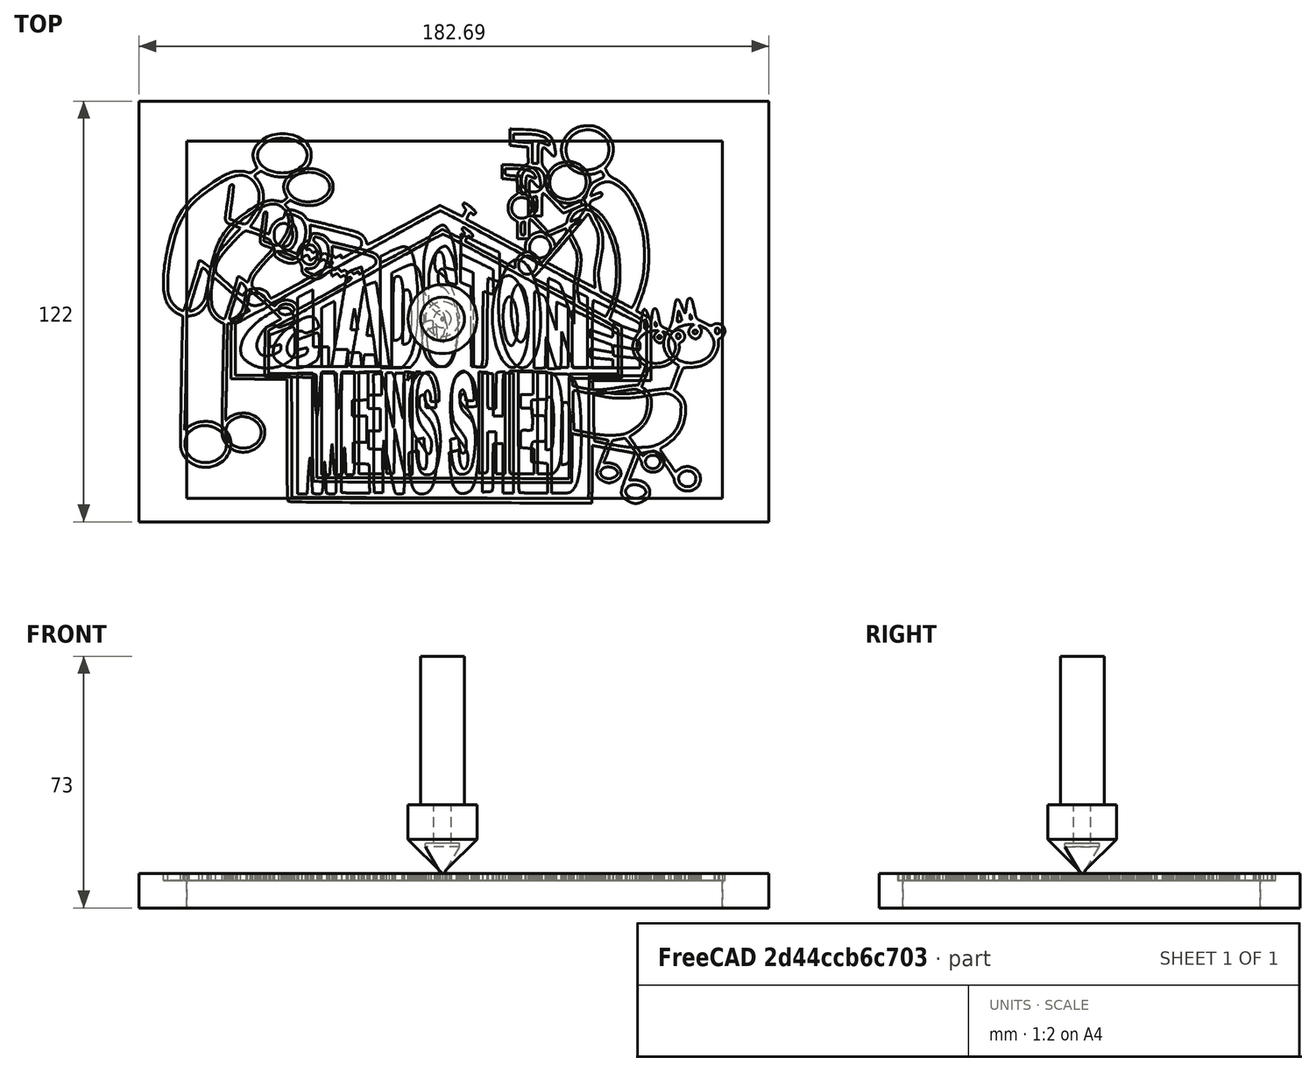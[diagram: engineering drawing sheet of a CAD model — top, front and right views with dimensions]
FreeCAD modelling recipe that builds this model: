
FCSTD DOCUMENT  (FreeCAD 0.19RUnknown)
Label: MensShedLogoVBit
License: All rights reserved
LicenseURL: http://en.wikipedia.org/wiki/All_rights_reserved
objects: Sketcher::SketchObject×20, PartDesign::Pocket×19, Path::FeaturePython×12, Part::FeaturePython×11, App::DocumentObjectGroup×6, App::FeaturePython×3, Path::FeatureCompoundPython×3, Mesh::FeaturePython×2, PartDesign::Pad×1, PartDesign::Body×1
note: 72 computed .brp shape members not serialized (recipe doc carries the construction recipe); baked Part::Feature solids carry a one-line shape summary decoded from their .brp

FEATURE [Sketcher::SketchObject] Sketch  label="M"
  FullyConstrained = false
  sketch-geometry (26):
    g0: BSplineCurve PolesCount=2 KnotsCount=2 Degree=1 IsPeriodic=0
    g1: BSplineCurve PolesCount=2 KnotsCount=2 Degree=1 IsPeriodic=0
    g2: BSplineCurve PolesCount=2 KnotsCount=2 Degree=1 IsPeriodic=0
    g3: BSplineCurve PolesCount=2 KnotsCount=2 Degree=1 IsPeriodic=0
    g4: BSplineCurve PolesCount=4 KnotsCount=2 Degree=3 IsPeriodic=0
    g5: BSplineCurve PolesCount=4 KnotsCount=2 Degree=3 IsPeriodic=0
    g6: BSplineCurve PolesCount=4 KnotsCount=2 Degree=3 IsPeriodic=0
    g7: BSplineCurve PolesCount=2 KnotsCount=2 Degree=1 IsPeriodic=0
    g8: BSplineCurve PolesCount=2 KnotsCount=2 Degree=1 IsPeriodic=0
    g9: BSplineCurve PolesCount=2 KnotsCount=2 Degree=1 IsPeriodic=0
    g10: BSplineCurve PolesCount=2 KnotsCount=2 Degree=1 IsPeriodic=0
    g11: BSplineCurve PolesCount=4 KnotsCount=2 Degree=3 IsPeriodic=0
    g12: BSplineCurve PolesCount=4 KnotsCount=2 Degree=3 IsPeriodic=0
    g13: BSplineCurve PolesCount=2 KnotsCount=2 Degree=1 IsPeriodic=0
    g14: BSplineCurve PolesCount=2 KnotsCount=2 Degree=1 IsPeriodic=0
    g15: BSplineCurve PolesCount=4 KnotsCount=2 Degree=3 IsPeriodic=0
    g16: BSplineCurve PolesCount=4 KnotsCount=2 Degree=3 IsPeriodic=0
    g17: BSplineCurve PolesCount=4 KnotsCount=2 Degree=3 IsPeriodic=0
    g18: BSplineCurve PolesCount=2 KnotsCount=2 Degree=1 IsPeriodic=0
    g19: BSplineCurve PolesCount=2 KnotsCount=2 Degree=1 IsPeriodic=0
    g20: BSplineCurve PolesCount=4 KnotsCount=2 Degree=3 IsPeriodic=0
    g21: BSplineCurve PolesCount=4 KnotsCount=2 Degree=3 IsPeriodic=0
    g22: BSplineCurve PolesCount=2 KnotsCount=2 Degree=1 IsPeriodic=0
    g23: BSplineCurve PolesCount=2 KnotsCount=2 Degree=1 IsPeriodic=0
    g24: BSplineCurve PolesCount=2 KnotsCount=2 Degree=1 IsPeriodic=0
    g25: BSplineCurve PolesCount=2 KnotsCount=2 Degree=1 IsPeriodic=0
  constraints (26):
    c: Coincident(g0,g1)
    c: Coincident(g1,g2)
    c: Coincident(g2,g3)
    c: Coincident(g3,g4)
    c: Coincident(g4,g5)
    c: Coincident(g5,g6)
    c: Coincident(g6,g7)
    c: Coincident(g7,g8)
    c: Coincident(g8,g9)
    c: Coincident(g9,g10)
    c: Coincident(g10,g11)
    c: Coincident(g11,g12)
    c: Coincident(g12,g13)
    c: Coincident(g13,g14)
    c: Coincident(g14,g15)
    c: Coincident(g15,g16)
    c: Coincident(g16,g17)
    c: Coincident(g17,g18)
    c: Coincident(g18,g19)
    c: Coincident(g19,g20)
    c: Coincident(g20,g21)
    c: Coincident(g21,g22)
    c: Coincident(g22,g23)
    c: Coincident(g23,g24)
    c: Coincident(g24,g25)
    c: Coincident(g25,g0)
FEATURE [Sketcher::SketchObject] Sketch001  label="N"
  FullyConstrained = false
  sketch-geometry (21):
    g0: BSplineCurve PolesCount=4 KnotsCount=2 Degree=3 IsPeriodic=0
    g1: BSplineCurve PolesCount=2 KnotsCount=2 Degree=1 IsPeriodic=0
    g2: BSplineCurve PolesCount=2 KnotsCount=2 Degree=1 IsPeriodic=0
    g3: BSplineCurve PolesCount=2 KnotsCount=2 Degree=1 IsPeriodic=0
    g4: BSplineCurve PolesCount=2 KnotsCount=2 Degree=1 IsPeriodic=0
    g5: BSplineCurve PolesCount=2 KnotsCount=2 Degree=1 IsPeriodic=0
    g6: BSplineCurve PolesCount=2 KnotsCount=2 Degree=1 IsPeriodic=0
    g7: BSplineCurve PolesCount=2 KnotsCount=2 Degree=1 IsPeriodic=0
    g8: BSplineCurve PolesCount=2 KnotsCount=2 Degree=1 IsPeriodic=0
    g9: BSplineCurve PolesCount=4 KnotsCount=2 Degree=3 IsPeriodic=0
    g10: BSplineCurve PolesCount=4 KnotsCount=2 Degree=3 IsPeriodic=0
    g11: BSplineCurve PolesCount=4 KnotsCount=2 Degree=3 IsPeriodic=0
    g12: BSplineCurve PolesCount=4 KnotsCount=2 Degree=3 IsPeriodic=0
    g13: BSplineCurve PolesCount=2 KnotsCount=2 Degree=1 IsPeriodic=0
    g14: BSplineCurve PolesCount=2 KnotsCount=2 Degree=1 IsPeriodic=0
    g15: BSplineCurve PolesCount=4 KnotsCount=2 Degree=3 IsPeriodic=0
    g16: BSplineCurve PolesCount=4 KnotsCount=2 Degree=3 IsPeriodic=0
    g17: BSplineCurve PolesCount=2 KnotsCount=2 Degree=1 IsPeriodic=0
    g18: BSplineCurve PolesCount=2 KnotsCount=2 Degree=1 IsPeriodic=0
    g19: BSplineCurve PolesCount=4 KnotsCount=2 Degree=3 IsPeriodic=0
    g20: BSplineCurve PolesCount=2 KnotsCount=2 Degree=1 IsPeriodic=0
  constraints (21):
    c: Coincident(g0,g1)
    c: Coincident(g1,g2)
    c: Coincident(g2,g3)
    c: Coincident(g3,g4)
    c: Coincident(g4,g5)
    c: Coincident(g5,g6)
    c: Coincident(g6,g7)
    c: Coincident(g7,g8)
    c: Coincident(g8,g9)
    c: Coincident(g9,g10)
    c: Coincident(g10,g11)
    c: Coincident(g11,g12)
    c: Coincident(g12,g13)
    c: Coincident(g13,g14)
    c: Coincident(g14,g15)
    c: Coincident(g15,g16)
    c: Coincident(g16,g17)
    c: Coincident(g17,g18)
    c: Coincident(g18,g19)
    c: Coincident(g19,g20)
    c: Coincident(g20,g0)
FEATURE [Sketcher::SketchObject] Sketch002  label="S"
  FullyConstrained = false
  sketch-geometry (25):
    g0: BSplineCurve PolesCount=4 KnotsCount=2 Degree=3 IsPeriodic=0
    g1: BSplineCurve PolesCount=4 KnotsCount=2 Degree=3 IsPeriodic=0
    g2: BSplineCurve PolesCount=4 KnotsCount=2 Degree=3 IsPeriodic=0
    g3: BSplineCurve PolesCount=2 KnotsCount=2 Degree=1 IsPeriodic=0
    g4: BSplineCurve PolesCount=2 KnotsCount=2 Degree=1 IsPeriodic=0
    g5: BSplineCurve PolesCount=4 KnotsCount=2 Degree=3 IsPeriodic=0
    g6: BSplineCurve PolesCount=4 KnotsCount=2 Degree=3 IsPeriodic=0
    g7: BSplineCurve PolesCount=4 KnotsCount=2 Degree=3 IsPeriodic=0
    g8: BSplineCurve PolesCount=4 KnotsCount=2 Degree=3 IsPeriodic=0
    g9: BSplineCurve PolesCount=4 KnotsCount=2 Degree=3 IsPeriodic=0
    g10: BSplineCurve PolesCount=4 KnotsCount=2 Degree=3 IsPeriodic=0
    g11: BSplineCurve PolesCount=4 KnotsCount=2 Degree=3 IsPeriodic=0
    g12: BSplineCurve PolesCount=4 KnotsCount=2 Degree=3 IsPeriodic=0
    g13: BSplineCurve PolesCount=2 KnotsCount=2 Degree=1 IsPeriodic=0
    g14: BSplineCurve PolesCount=2 KnotsCount=2 Degree=1 IsPeriodic=0
    g15: BSplineCurve PolesCount=2 KnotsCount=2 Degree=1 IsPeriodic=0
    g16: BSplineCurve PolesCount=2 KnotsCount=2 Degree=1 IsPeriodic=0
    g17: BSplineCurve PolesCount=4 KnotsCount=2 Degree=3 IsPeriodic=0
    g18: BSplineCurve PolesCount=4 KnotsCount=2 Degree=3 IsPeriodic=0
    g19: BSplineCurve PolesCount=4 KnotsCount=2 Degree=3 IsPeriodic=0
    g20: BSplineCurve PolesCount=4 KnotsCount=2 Degree=3 IsPeriodic=0
    g21: BSplineCurve PolesCount=4 KnotsCount=2 Degree=3 IsPeriodic=0
    g22: BSplineCurve PolesCount=4 KnotsCount=2 Degree=3 IsPeriodic=0
    g23: BSplineCurve PolesCount=4 KnotsCount=2 Degree=3 IsPeriodic=0
    g24: BSplineCurve PolesCount=2 KnotsCount=2 Degree=1 IsPeriodic=0
  constraints (25):
    c: Coincident(g0,g1)
    c: Coincident(g1,g2)
    c: Coincident(g2,g3)
    c: Coincident(g3,g4)
    c: Coincident(g4,g5)
    c: Coincident(g5,g6)
    c: Coincident(g6,g7)
    c: Coincident(g7,g8)
    c: Coincident(g8,g9)
    c: Coincident(g9,g10)
    c: Coincident(g10,g11)
    c: Coincident(g11,g12)
    c: Coincident(g12,g13)
    c: Coincident(g13,g14)
    c: Coincident(g14,g15)
    c: Coincident(g15,g16)
    c: Coincident(g16,g17)
    c: Coincident(g17,g18)
    c: Coincident(g18,g19)
    c: Coincident(g19,g20)
    c: Coincident(g20,g21)
    c: Coincident(g21,g22)
    c: Coincident(g22,g23)
    c: Coincident(g23,g24)
    c: Coincident(g24,g0)
FEATURE [Sketcher::SketchObject] Sketch003  label="S001"
  FullyConstrained = false
  sketch-geometry (24):
    g0: BSplineCurve PolesCount=4 KnotsCount=2 Degree=3 IsPeriodic=0
    g1: BSplineCurve PolesCount=2 KnotsCount=2 Degree=1 IsPeriodic=0
    g2: BSplineCurve PolesCount=2 KnotsCount=2 Degree=1 IsPeriodic=0
    g3: BSplineCurve PolesCount=4 KnotsCount=2 Degree=3 IsPeriodic=0
    g4: BSplineCurve PolesCount=4 KnotsCount=2 Degree=3 IsPeriodic=0
    g5: BSplineCurve PolesCount=4 KnotsCount=2 Degree=3 IsPeriodic=0
    g6: BSplineCurve PolesCount=4 KnotsCount=2 Degree=3 IsPeriodic=0
    g7: BSplineCurve PolesCount=4 KnotsCount=2 Degree=3 IsPeriodic=0
    g8: BSplineCurve PolesCount=4 KnotsCount=2 Degree=3 IsPeriodic=0
    g9: BSplineCurve PolesCount=4 KnotsCount=2 Degree=3 IsPeriodic=0
    g10: BSplineCurve PolesCount=4 KnotsCount=2 Degree=3 IsPeriodic=0
    g11: BSplineCurve PolesCount=4 KnotsCount=2 Degree=3 IsPeriodic=0
    g12: BSplineCurve PolesCount=4 KnotsCount=2 Degree=3 IsPeriodic=0
    g13: BSplineCurve PolesCount=4 KnotsCount=2 Degree=3 IsPeriodic=0
    g14: BSplineCurve PolesCount=2 KnotsCount=2 Degree=1 IsPeriodic=0
    g15: BSplineCurve PolesCount=2 KnotsCount=2 Degree=1 IsPeriodic=0
    g16: BSplineCurve PolesCount=4 KnotsCount=2 Degree=3 IsPeriodic=0
    g17: BSplineCurve PolesCount=4 KnotsCount=2 Degree=3 IsPeriodic=0
    g18: BSplineCurve PolesCount=4 KnotsCount=2 Degree=3 IsPeriodic=0
    g19: BSplineCurve PolesCount=4 KnotsCount=2 Degree=3 IsPeriodic=0
    g20: BSplineCurve PolesCount=4 KnotsCount=2 Degree=3 IsPeriodic=0
    g21: BSplineCurve PolesCount=4 KnotsCount=2 Degree=3 IsPeriodic=0
    g22: BSplineCurve PolesCount=4 KnotsCount=2 Degree=3 IsPeriodic=0
    g23: BSplineCurve PolesCount=2 KnotsCount=2 Degree=1 IsPeriodic=0
  constraints (24):
    c: Coincident(g0,g1)
    c: Coincident(g1,g2)
    c: Coincident(g2,g3)
    c: Coincident(g3,g4)
    c: Coincident(g4,g5)
    c: Coincident(g5,g6)
    c: Coincident(g6,g7)
    c: Coincident(g7,g8)
    c: Coincident(g8,g9)
    c: Coincident(g9,g10)
    c: Coincident(g10,g11)
    c: Coincident(g11,g12)
    c: Coincident(g12,g13)
    c: Coincident(g13,g14)
    c: Coincident(g14,g15)
    c: Coincident(g15,g16)
    c: Coincident(g16,g17)
    c: Coincident(g17,g18)
    c: Coincident(g18,g19)
    c: Coincident(g19,g20)
    c: Coincident(g20,g21)
    c: Coincident(g21,g22)
    c: Coincident(g22,g23)
    c: Coincident(g23,g0)
FEATURE [Sketcher::SketchObject] Sketch004  label="E"
  FullyConstrained = false
  sketch-geometry (24):
    g0: BSplineCurve PolesCount=4 KnotsCount=2 Degree=3 IsPeriodic=0
    g1: BSplineCurve PolesCount=4 KnotsCount=2 Degree=3 IsPeriodic=0
    g2: BSplineCurve PolesCount=2 KnotsCount=2 Degree=1 IsPeriodic=0
    g3: BSplineCurve PolesCount=2 KnotsCount=2 Degree=1 IsPeriodic=0
    g4: BSplineCurve PolesCount=2 KnotsCount=2 Degree=1 IsPeriodic=0
    g5: BSplineCurve PolesCount=2 KnotsCount=2 Degree=1 IsPeriodic=0
    g6: BSplineCurve PolesCount=2 KnotsCount=2 Degree=1 IsPeriodic=0
    g7: BSplineCurve PolesCount=2 KnotsCount=2 Degree=1 IsPeriodic=0
    g8: BSplineCurve PolesCount=2 KnotsCount=2 Degree=1 IsPeriodic=0
    g9: BSplineCurve PolesCount=2 KnotsCount=2 Degree=1 IsPeriodic=0
    g10: BSplineCurve PolesCount=2 KnotsCount=2 Degree=1 IsPeriodic=0
    g11: BSplineCurve PolesCount=2 KnotsCount=2 Degree=1 IsPeriodic=0
    g12: BSplineCurve PolesCount=2 KnotsCount=2 Degree=1 IsPeriodic=0
    g13: BSplineCurve PolesCount=2 KnotsCount=2 Degree=1 IsPeriodic=0
    g14: BSplineCurve PolesCount=2 KnotsCount=2 Degree=1 IsPeriodic=0
    g15: BSplineCurve PolesCount=2 KnotsCount=2 Degree=1 IsPeriodic=0
    g16: BSplineCurve PolesCount=2 KnotsCount=2 Degree=1 IsPeriodic=0
    g17: BSplineCurve PolesCount=2 KnotsCount=2 Degree=1 IsPeriodic=0
    g18: BSplineCurve PolesCount=2 KnotsCount=2 Degree=1 IsPeriodic=0
    g19: BSplineCurve PolesCount=2 KnotsCount=2 Degree=1 IsPeriodic=0
    g20: BSplineCurve PolesCount=2 KnotsCount=2 Degree=1 IsPeriodic=0
    g21: BSplineCurve PolesCount=2 KnotsCount=2 Degree=1 IsPeriodic=0
    g22: BSplineCurve PolesCount=4 KnotsCount=2 Degree=3 IsPeriodic=0
    g23: BSplineCurve PolesCount=2 KnotsCount=2 Degree=1 IsPeriodic=0
  constraints (24):
    c: Coincident(g0,g1)
    c: Coincident(g1,g2)
    c: Coincident(g2,g3)
    c: Coincident(g3,g4)
    c: Coincident(g4,g5)
    c: Coincident(g5,g6)
    c: Coincident(g6,g7)
    c: Coincident(g7,g8)
    c: Coincident(g8,g9)
    c: Coincident(g9,g10)
    c: Coincident(g10,g11)
    c: Coincident(g11,g12)
    c: Coincident(g12,g13)
    c: Coincident(g13,g14)
    c: Coincident(g14,g15)
    c: Coincident(g15,g16)
    c: Coincident(g16,g17)
    c: Coincident(g17,g18)
    c: Coincident(g18,g19)
    c: Coincident(g19,g20)
    c: Coincident(g20,g21)
    c: Coincident(g21,g22)
    c: Coincident(g22,g23)
    c: Coincident(g23,g0)
FEATURE [Sketcher::SketchObject] Sketch005  label="H"
  FullyConstrained = false
  sketch-geometry (24):
    g0: BSplineCurve PolesCount=2 KnotsCount=2 Degree=1 IsPeriodic=0
    g1: BSplineCurve PolesCount=2 KnotsCount=2 Degree=1 IsPeriodic=0
    g2: BSplineCurve PolesCount=2 KnotsCount=2 Degree=1 IsPeriodic=0
    g3: BSplineCurve PolesCount=2 KnotsCount=2 Degree=1 IsPeriodic=0
    g4: BSplineCurve PolesCount=4 KnotsCount=2 Degree=3 IsPeriodic=0
    g5: BSplineCurve PolesCount=4 KnotsCount=2 Degree=3 IsPeriodic=0
    g6: BSplineCurve PolesCount=2 KnotsCount=2 Degree=1 IsPeriodic=0
    g7: BSplineCurve PolesCount=2 KnotsCount=2 Degree=1 IsPeriodic=0
    g8: BSplineCurve PolesCount=2 KnotsCount=2 Degree=1 IsPeriodic=0
    g9: BSplineCurve PolesCount=2 KnotsCount=2 Degree=1 IsPeriodic=0
    g10: BSplineCurve PolesCount=2 KnotsCount=2 Degree=1 IsPeriodic=0
    g11: BSplineCurve PolesCount=2 KnotsCount=2 Degree=1 IsPeriodic=0
    g12: BSplineCurve PolesCount=2 KnotsCount=2 Degree=1 IsPeriodic=0
    g13: BSplineCurve PolesCount=2 KnotsCount=2 Degree=1 IsPeriodic=0
    g14: BSplineCurve PolesCount=2 KnotsCount=2 Degree=1 IsPeriodic=0
    g15: BSplineCurve PolesCount=2 KnotsCount=2 Degree=1 IsPeriodic=0
    g16: BSplineCurve PolesCount=4 KnotsCount=2 Degree=3 IsPeriodic=0
    g17: BSplineCurve PolesCount=4 KnotsCount=2 Degree=3 IsPeriodic=0
    g18: BSplineCurve PolesCount=2 KnotsCount=2 Degree=1 IsPeriodic=0
    g19: BSplineCurve PolesCount=2 KnotsCount=2 Degree=1 IsPeriodic=0
    g20: BSplineCurve PolesCount=2 KnotsCount=2 Degree=1 IsPeriodic=0
    g21: BSplineCurve PolesCount=2 KnotsCount=2 Degree=1 IsPeriodic=0
    g22: BSplineCurve PolesCount=2 KnotsCount=2 Degree=1 IsPeriodic=0
    g23: BSplineCurve PolesCount=2 KnotsCount=2 Degree=1 IsPeriodic=0
  constraints (24):
    c: Coincident(g0,g1)
    c: Coincident(g1,g2)
    c: Coincident(g2,g3)
    c: Coincident(g3,g4)
    c: Coincident(g4,g5)
    c: Coincident(g5,g6)
    c: Coincident(g6,g7)
    c: Coincident(g7,g8)
    c: Coincident(g8,g9)
    c: Coincident(g9,g10)
    c: Coincident(g10,g11)
    c: Coincident(g11,g12)
    c: Coincident(g12,g13)
    c: Coincident(g13,g14)
    c: Coincident(g14,g15)
    c: Coincident(g15,g16)
    c: Coincident(g16,g17)
    c: Coincident(g17,g18)
    c: Coincident(g18,g19)
    c: Coincident(g19,g20)
    c: Coincident(g20,g21)
    c: Coincident(g21,g22)
    c: Coincident(g22,g23)
    c: Coincident(g23,g0)
FEATURE [Sketcher::SketchObject] Sketch006  label="E001"
  FullyConstrained = false
  sketch-geometry (24):
    g0: BSplineCurve PolesCount=4 KnotsCount=2 Degree=3 IsPeriodic=0
    g1: BSplineCurve PolesCount=2 KnotsCount=2 Degree=1 IsPeriodic=0
    g2: BSplineCurve PolesCount=2 KnotsCount=2 Degree=1 IsPeriodic=0
    g3: BSplineCurve PolesCount=2 KnotsCount=2 Degree=1 IsPeriodic=0
    g4: BSplineCurve PolesCount=2 KnotsCount=2 Degree=1 IsPeriodic=0
    g5: BSplineCurve PolesCount=2 KnotsCount=2 Degree=1 IsPeriodic=0
    g6: BSplineCurve PolesCount=2 KnotsCount=2 Degree=1 IsPeriodic=0
    g7: BSplineCurve PolesCount=2 KnotsCount=2 Degree=1 IsPeriodic=0
    g8: BSplineCurve PolesCount=2 KnotsCount=2 Degree=1 IsPeriodic=0
    g9: BSplineCurve PolesCount=4 KnotsCount=2 Degree=3 IsPeriodic=0
    g10: BSplineCurve PolesCount=4 KnotsCount=2 Degree=3 IsPeriodic=0
    g11: BSplineCurve PolesCount=4 KnotsCount=2 Degree=3 IsPeriodic=0
    g12: BSplineCurve PolesCount=4 KnotsCount=2 Degree=3 IsPeriodic=0
    g13: BSplineCurve PolesCount=4 KnotsCount=2 Degree=3 IsPeriodic=0
    g14: BSplineCurve PolesCount=4 KnotsCount=2 Degree=3 IsPeriodic=0
    g15: BSplineCurve PolesCount=2 KnotsCount=2 Degree=1 IsPeriodic=0
    g16: BSplineCurve PolesCount=2 KnotsCount=2 Degree=1 IsPeriodic=0
    g17: BSplineCurve PolesCount=4 KnotsCount=2 Degree=3 IsPeriodic=0
    g18: BSplineCurve PolesCount=2 KnotsCount=2 Degree=1 IsPeriodic=0
    g19: BSplineCurve PolesCount=2 KnotsCount=2 Degree=1 IsPeriodic=0
    g20: BSplineCurve PolesCount=2 KnotsCount=2 Degree=1 IsPeriodic=0
    g21: BSplineCurve PolesCount=2 KnotsCount=2 Degree=1 IsPeriodic=0
    g22: BSplineCurve PolesCount=4 KnotsCount=2 Degree=3 IsPeriodic=0
    g23: BSplineCurve PolesCount=2 KnotsCount=2 Degree=1 IsPeriodic=0
  constraints (24):
    c: Coincident(g0,g1)
    c: Coincident(g1,g2)
    c: Coincident(g2,g3)
    c: Coincident(g3,g4)
    c: Coincident(g4,g5)
    c: Coincident(g5,g6)
    c: Coincident(g6,g7)
    c: Coincident(g7,g8)
    c: Coincident(g8,g9)
    c: Coincident(g9,g10)
    c: Coincident(g10,g11)
    c: Coincident(g11,g12)
    c: Coincident(g12,g13)
    c: Coincident(g13,g14)
    c: Coincident(g14,g15)
    c: Coincident(g15,g16)
    c: Coincident(g16,g17)
    c: Coincident(g17,g18)
    c: Coincident(g18,g19)
    c: Coincident(g19,g20)
    c: Coincident(g20,g21)
    c: Coincident(g21,g22)
    c: Coincident(g22,g23)
    c: Coincident(g23,g0)
FEATURE [Sketcher::SketchObject] Sketch007  label="D"
  FullyConstrained = false
  sketch-geometry (17):
    g0: BSplineCurve PolesCount=2 KnotsCount=2 Degree=1 IsPeriodic=0
    g1: BSplineCurve PolesCount=2 KnotsCount=2 Degree=1 IsPeriodic=0
    g2: BSplineCurve PolesCount=4 KnotsCount=2 Degree=3 IsPeriodic=0
    g3: BSplineCurve PolesCount=4 KnotsCount=2 Degree=3 IsPeriodic=0
    g4: BSplineCurve PolesCount=4 KnotsCount=2 Degree=3 IsPeriodic=0
    g5: BSplineCurve PolesCount=4 KnotsCount=2 Degree=3 IsPeriodic=0
    g6: BSplineCurve PolesCount=2 KnotsCount=2 Degree=1 IsPeriodic=0
    g7: BSplineCurve PolesCount=2 KnotsCount=2 Degree=1 IsPeriodic=0
    g8: BSplineCurve PolesCount=4 KnotsCount=2 Degree=3 IsPeriodic=0
    g9: BSplineCurve PolesCount=4 KnotsCount=2 Degree=3 IsPeriodic=0
    g10: BSplineCurve PolesCount=2 KnotsCount=2 Degree=1 IsPeriodic=0
    g11: BSplineCurve PolesCount=2 KnotsCount=2 Degree=1 IsPeriodic=0
    g12: BSplineCurve PolesCount=4 KnotsCount=2 Degree=3 IsPeriodic=0
    g13: BSplineCurve PolesCount=2 KnotsCount=2 Degree=1 IsPeriodic=0
    g14: BSplineCurve PolesCount=2 KnotsCount=2 Degree=1 IsPeriodic=0
    g15: BSplineCurve PolesCount=4 KnotsCount=2 Degree=3 IsPeriodic=0
    g16: BSplineCurve PolesCount=2 KnotsCount=2 Degree=1 IsPeriodic=0
  constraints (17):
    c: Coincident(g0,g1)
    c: Coincident(g1,g2)
    c: Coincident(g2,g3)
    c: Coincident(g3,g4)
    c: Coincident(g4,g5)
    c: Coincident(g5,g6)
    c: Coincident(g6,g7)
    c: Coincident(g7,g0)
    c: Coincident(g8,g9)
    c: Coincident(g9,g10)
    c: Coincident(g10,g11)
    c: Coincident(g11,g12)
    c: Coincident(g12,g13)
    c: Coincident(g13,g14)
    c: Coincident(g14,g15)
    c: Coincident(g15,g16)
    c: Coincident(g16,g8)
FEATURE [Sketcher::SketchObject] Sketch008  label="G"
  FullyConstrained = false
  sketch-geometry (24):
    g0: BSplineCurve PolesCount=4 KnotsCount=2 Degree=3 IsPeriodic=0
    g1: BSplineCurve PolesCount=4 KnotsCount=2 Degree=3 IsPeriodic=0
    g2: BSplineCurve PolesCount=4 KnotsCount=2 Degree=3 IsPeriodic=0
    g3: BSplineCurve PolesCount=4 KnotsCount=2 Degree=3 IsPeriodic=0
    g4: BSplineCurve PolesCount=4 KnotsCount=2 Degree=3 IsPeriodic=0
    g5: BSplineCurve PolesCount=4 KnotsCount=2 Degree=3 IsPeriodic=0
    g6: BSplineCurve PolesCount=4 KnotsCount=2 Degree=3 IsPeriodic=0
    g7: BSplineCurve PolesCount=4 KnotsCount=2 Degree=3 IsPeriodic=0
    g8: BSplineCurve PolesCount=4 KnotsCount=2 Degree=3 IsPeriodic=0
    g9: BSplineCurve PolesCount=4 KnotsCount=2 Degree=3 IsPeriodic=0
    g10: BSplineCurve PolesCount=4 KnotsCount=2 Degree=3 IsPeriodic=0
    g11: BSplineCurve PolesCount=4 KnotsCount=2 Degree=3 IsPeriodic=0
    g12: BSplineCurve PolesCount=4 KnotsCount=2 Degree=3 IsPeriodic=0
    g13: BSplineCurve PolesCount=4 KnotsCount=2 Degree=3 IsPeriodic=0
    g14: BSplineCurve PolesCount=2 KnotsCount=2 Degree=1 IsPeriodic=0
    g15: BSplineCurve PolesCount=2 KnotsCount=2 Degree=1 IsPeriodic=0
    g16: BSplineCurve PolesCount=2 KnotsCount=2 Degree=1 IsPeriodic=0
    g17: BSplineCurve PolesCount=2 KnotsCount=2 Degree=1 IsPeriodic=0
    g18: BSplineCurve PolesCount=4 KnotsCount=2 Degree=3 IsPeriodic=0
    g19: BSplineCurve PolesCount=4 KnotsCount=2 Degree=3 IsPeriodic=0
    g20: BSplineCurve PolesCount=2 KnotsCount=2 Degree=1 IsPeriodic=0
    g21: BSplineCurve PolesCount=2 KnotsCount=2 Degree=1 IsPeriodic=0
    g22: BSplineCurve PolesCount=4 KnotsCount=2 Degree=3 IsPeriodic=0
    g23: BSplineCurve PolesCount=2 KnotsCount=2 Degree=1 IsPeriodic=0
  constraints (24):
    c: Coincident(g0,g1)
    c: Coincident(g1,g2)
    c: Coincident(g2,g3)
    c: Coincident(g3,g4)
    c: Coincident(g4,g5)
    c: Coincident(g5,g6)
    c: Coincident(g6,g7)
    c: Coincident(g7,g8)
    c: Coincident(g8,g9)
    c: Coincident(g9,g10)
    c: Coincident(g10,g11)
    c: Coincident(g11,g12)
    c: Coincident(g12,g13)
    c: Coincident(g13,g14)
    c: Coincident(g14,g15)
    c: Coincident(g15,g16)
    c: Coincident(g16,g17)
    c: Coincident(g17,g18)
    c: Coincident(g18,g19)
    c: Coincident(g19,g20)
    c: Coincident(g20,g21)
    c: Coincident(g21,g22)
    c: Coincident(g22,g23)
    c: Coincident(g23,g0)
FEATURE [Sketcher::SketchObject] Sketch009  label="N001"
  FullyConstrained = false
  sketch-geometry (21):
    g0: BSplineCurve PolesCount=4 KnotsCount=2 Degree=3 IsPeriodic=0
    g1: BSplineCurve PolesCount=4 KnotsCount=2 Degree=3 IsPeriodic=0
    g2: BSplineCurve PolesCount=4 KnotsCount=2 Degree=3 IsPeriodic=0
    g3: BSplineCurve PolesCount=4 KnotsCount=2 Degree=3 IsPeriodic=0
    g4: BSplineCurve PolesCount=2 KnotsCount=2 Degree=1 IsPeriodic=0
    g5: BSplineCurve PolesCount=2 KnotsCount=2 Degree=1 IsPeriodic=0
    g6: BSplineCurve PolesCount=4 KnotsCount=2 Degree=3 IsPeriodic=0
    g7: BSplineCurve PolesCount=4 KnotsCount=2 Degree=3 IsPeriodic=0
    g8: BSplineCurve PolesCount=2 KnotsCount=2 Degree=1 IsPeriodic=0
    g9: BSplineCurve PolesCount=2 KnotsCount=2 Degree=1 IsPeriodic=0
    g10: BSplineCurve PolesCount=2 KnotsCount=2 Degree=1 IsPeriodic=0
    g11: BSplineCurve PolesCount=2 KnotsCount=2 Degree=1 IsPeriodic=0
    g12: BSplineCurve PolesCount=2 KnotsCount=2 Degree=1 IsPeriodic=0
    g13: BSplineCurve PolesCount=2 KnotsCount=2 Degree=1 IsPeriodic=0
    g14: BSplineCurve PolesCount=2 KnotsCount=2 Degree=1 IsPeriodic=0
    g15: BSplineCurve PolesCount=2 KnotsCount=2 Degree=1 IsPeriodic=0
    g16: BSplineCurve PolesCount=2 KnotsCount=2 Degree=1 IsPeriodic=0
    g17: BSplineCurve PolesCount=2 KnotsCount=2 Degree=1 IsPeriodic=0
    g18: BSplineCurve PolesCount=2 KnotsCount=2 Degree=1 IsPeriodic=0
    g19: BSplineCurve PolesCount=2 KnotsCount=2 Degree=1 IsPeriodic=0
    g20: BSplineCurve PolesCount=2 KnotsCount=2 Degree=1 IsPeriodic=0
  constraints (21):
    c: Coincident(g0,g1)
    c: Coincident(g1,g2)
    c: Coincident(g2,g3)
    c: Coincident(g3,g4)
    c: Coincident(g4,g5)
    c: Coincident(g5,g6)
    c: Coincident(g6,g7)
    c: Coincident(g7,g8)
    c: Coincident(g8,g9)
    c: Coincident(g9,g10)
    c: Coincident(g10,g11)
    c: Coincident(g11,g12)
    c: Coincident(g12,g13)
    c: Coincident(g13,g14)
    c: Coincident(g14,g15)
    c: Coincident(g15,g16)
    c: Coincident(g16,g17)
    c: Coincident(g17,g18)
    c: Coincident(g18,g19)
    c: Coincident(g19,g20)
    c: Coincident(g20,g0)
FEATURE [Sketcher::SketchObject] Sketch010  label="D001"
  FullyConstrained = false
  sketch-geometry (18):
    g0: BSplineCurve PolesCount=2 KnotsCount=2 Degree=1 IsPeriodic=0
    g1: BSplineCurve PolesCount=2 KnotsCount=2 Degree=1 IsPeriodic=0
    g2: BSplineCurve PolesCount=4 KnotsCount=2 Degree=3 IsPeriodic=0
    g3: BSplineCurve PolesCount=4 KnotsCount=2 Degree=3 IsPeriodic=0
    g4: BSplineCurve PolesCount=4 KnotsCount=2 Degree=3 IsPeriodic=0
    g5: BSplineCurve PolesCount=4 KnotsCount=2 Degree=3 IsPeriodic=0
    g6: BSplineCurve PolesCount=2 KnotsCount=2 Degree=1 IsPeriodic=0
    g7: BSplineCurve PolesCount=2 KnotsCount=2 Degree=1 IsPeriodic=0
    g8: BSplineCurve PolesCount=2 KnotsCount=2 Degree=1 IsPeriodic=0
    g9: BSplineCurve PolesCount=2 KnotsCount=2 Degree=1 IsPeriodic=0
    g10: BSplineCurve PolesCount=4 KnotsCount=2 Degree=3 IsPeriodic=0
    g11: BSplineCurve PolesCount=4 KnotsCount=2 Degree=3 IsPeriodic=0
    g12: BSplineCurve PolesCount=4 KnotsCount=2 Degree=3 IsPeriodic=0
    g13: BSplineCurve PolesCount=4 KnotsCount=2 Degree=3 IsPeriodic=0
    g14: BSplineCurve PolesCount=4 KnotsCount=2 Degree=3 IsPeriodic=0
    g15: BSplineCurve PolesCount=2 KnotsCount=2 Degree=1 IsPeriodic=0
    g16: BSplineCurve PolesCount=2 KnotsCount=2 Degree=1 IsPeriodic=0
    g17: BSplineCurve PolesCount=4 KnotsCount=2 Degree=3 IsPeriodic=0
  constraints (18):
    c: Coincident(g0,g1)
    c: Coincident(g1,g2)
    c: Coincident(g2,g3)
    c: Coincident(g3,g4)
    c: Coincident(g4,g5)
    c: Coincident(g5,g6)
    c: Coincident(g6,g7)
    c: Coincident(g7,g8)
    c: Coincident(g8,g9)
    c: Coincident(g9,g0)
    c: Coincident(g10,g11)
    c: Coincident(g11,g12)
    c: Coincident(g12,g13)
    c: Coincident(g13,g14)
    c: Coincident(g14,g15)
    c: Coincident(g15,g16)
    c: Coincident(g16,g17)
    c: Coincident(g17,g10)
FEATURE [Sketcher::SketchObject] Sketch011  label="T"
  FullyConstrained = false
  sketch-geometry (16):
    g0: BSplineCurve PolesCount=2 KnotsCount=2 Degree=1 IsPeriodic=0
    g1: BSplineCurve PolesCount=2 KnotsCount=2 Degree=1 IsPeriodic=0
    g2: BSplineCurve PolesCount=2 KnotsCount=2 Degree=1 IsPeriodic=0
    g3: BSplineCurve PolesCount=2 KnotsCount=2 Degree=1 IsPeriodic=0
    g4: BSplineCurve PolesCount=2 KnotsCount=2 Degree=1 IsPeriodic=0
    g5: BSplineCurve PolesCount=2 KnotsCount=2 Degree=1 IsPeriodic=0
    g6: BSplineCurve PolesCount=2 KnotsCount=2 Degree=1 IsPeriodic=0
    g7: BSplineCurve PolesCount=2 KnotsCount=2 Degree=1 IsPeriodic=0
    g8: BSplineCurve PolesCount=4 KnotsCount=2 Degree=3 IsPeriodic=0
    g9: BSplineCurve PolesCount=2 KnotsCount=2 Degree=1 IsPeriodic=0
    g10: BSplineCurve PolesCount=2 KnotsCount=2 Degree=1 IsPeriodic=0
    g11: BSplineCurve PolesCount=4 KnotsCount=2 Degree=3 IsPeriodic=0
    g12: BSplineCurve PolesCount=4 KnotsCount=2 Degree=3 IsPeriodic=0
    g13: BSplineCurve PolesCount=4 KnotsCount=2 Degree=3 IsPeriodic=0
    g14: BSplineCurve PolesCount=4 KnotsCount=2 Degree=3 IsPeriodic=0
    g15: BSplineCurve PolesCount=2 KnotsCount=2 Degree=1 IsPeriodic=0
  constraints (16):
    c: Coincident(g0,g1)
    c: Coincident(g1,g2)
    c: Coincident(g2,g3)
    c: Coincident(g3,g4)
    c: Coincident(g4,g5)
    c: Coincident(g5,g6)
    c: Coincident(g6,g7)
    c: Coincident(g7,g8)
    c: Coincident(g8,g9)
    c: Coincident(g9,g10)
    c: Coincident(g10,g11)
    c: Coincident(g11,g12)
    c: Coincident(g12,g13)
    c: Coincident(g13,g14)
    c: Coincident(g14,g15)
    c: Coincident(g15,g0)
FEATURE [Sketcher::SketchObject] Sketch012  label="O"
  FullyConstrained = false
  sketch-geometry (8):
    g0: BSplineCurve PolesCount=4 KnotsCount=2 Degree=3 IsPeriodic=0
    g1: BSplineCurve PolesCount=4 KnotsCount=2 Degree=3 IsPeriodic=0
    g2: BSplineCurve PolesCount=4 KnotsCount=2 Degree=3 IsPeriodic=0
    g3: BSplineCurve PolesCount=4 KnotsCount=2 Degree=3 IsPeriodic=0
    g4: BSplineCurve PolesCount=4 KnotsCount=2 Degree=3 IsPeriodic=0
    g5: BSplineCurve PolesCount=4 KnotsCount=2 Degree=3 IsPeriodic=0
    g6: BSplineCurve PolesCount=4 KnotsCount=2 Degree=3 IsPeriodic=0
    g7: BSplineCurve PolesCount=4 KnotsCount=2 Degree=3 IsPeriodic=0
  constraints (8):
    c: Coincident(g0,g1)
    c: Coincident(g1,g2)
    c: Coincident(g2,g3)
    c: Coincident(g3,g0)
    c: Coincident(g4,g5)
    c: Coincident(g5,g6)
    c: Coincident(g6,g7)
    c: Coincident(g7,g4)
FEATURE [Sketcher::SketchObject] Sketch013  label="E002"
  FullyConstrained = false
  sketch-geometry (24):
    g0: BSplineCurve PolesCount=4 KnotsCount=2 Degree=3 IsPeriodic=0
    g1: BSplineCurve PolesCount=4 KnotsCount=2 Degree=3 IsPeriodic=0
    g2: BSplineCurve PolesCount=4 KnotsCount=2 Degree=3 IsPeriodic=0
    g3: BSplineCurve PolesCount=4 KnotsCount=2 Degree=3 IsPeriodic=0
    g4: BSplineCurve PolesCount=4 KnotsCount=2 Degree=3 IsPeriodic=0
    g5: BSplineCurve PolesCount=4 KnotsCount=2 Degree=3 IsPeriodic=0
    g6: BSplineCurve PolesCount=4 KnotsCount=2 Degree=3 IsPeriodic=0
    g7: BSplineCurve PolesCount=4 KnotsCount=2 Degree=3 IsPeriodic=0
    g8: BSplineCurve PolesCount=2 KnotsCount=2 Degree=1 IsPeriodic=0
    g9: BSplineCurve PolesCount=2 KnotsCount=2 Degree=1 IsPeriodic=0
    g10: BSplineCurve PolesCount=4 KnotsCount=2 Degree=3 IsPeriodic=0
    g11: BSplineCurve PolesCount=4 KnotsCount=2 Degree=3 IsPeriodic=0
    g12: BSplineCurve PolesCount=4 KnotsCount=2 Degree=3 IsPeriodic=0
    g13: BSplineCurve PolesCount=4 KnotsCount=2 Degree=3 IsPeriodic=0
    g14: BSplineCurve PolesCount=4 KnotsCount=2 Degree=3 IsPeriodic=0
    g15: BSplineCurve PolesCount=2 KnotsCount=2 Degree=1 IsPeriodic=0
    g16: BSplineCurve PolesCount=2 KnotsCount=2 Degree=1 IsPeriodic=0
    g17: BSplineCurve PolesCount=4 KnotsCount=2 Degree=3 IsPeriodic=0
    g18: BSplineCurve PolesCount=2 KnotsCount=2 Degree=1 IsPeriodic=0
    g19: BSplineCurve PolesCount=2 KnotsCount=2 Degree=1 IsPeriodic=0
    g20: BSplineCurve PolesCount=2 KnotsCount=2 Degree=1 IsPeriodic=0
    g21: BSplineCurve PolesCount=2 KnotsCount=2 Degree=1 IsPeriodic=0
    g22: BSplineCurve PolesCount=2 KnotsCount=2 Degree=1 IsPeriodic=0
    g23: BSplineCurve PolesCount=2 KnotsCount=2 Degree=1 IsPeriodic=0
  constraints (24):
    c: Coincident(g0,g1)
    c: Coincident(g1,g2)
    c: Coincident(g2,g3)
    c: Coincident(g3,g4)
    c: Coincident(g4,g5)
    c: Coincident(g5,g6)
    c: Coincident(g6,g7)
    c: Coincident(g7,g8)
    c: Coincident(g8,g9)
    c: Coincident(g9,g10)
    c: Coincident(g10,g11)
    c: Coincident(g11,g12)
    c: Coincident(g12,g13)
    c: Coincident(g13,g14)
    c: Coincident(g14,g15)
    c: Coincident(g15,g16)
    c: Coincident(g16,g17)
    c: Coincident(g17,g18)
    c: Coincident(g18,g19)
    c: Coincident(g19,g20)
    c: Coincident(g20,g21)
    c: Coincident(g21,g22)
    c: Coincident(g22,g23)
    c: Coincident(g23,g0)
FEATURE [Sketcher::SketchObject] Sketch014  label="L"
  FullyConstrained = false
  sketch-geometry (12):
    g0: BSplineCurve PolesCount=2 KnotsCount=2 Degree=1 IsPeriodic=0
    g1: BSplineCurve PolesCount=2 KnotsCount=2 Degree=1 IsPeriodic=0
    g2: BSplineCurve PolesCount=4 KnotsCount=2 Degree=3 IsPeriodic=0
    g3: BSplineCurve PolesCount=4 KnotsCount=2 Degree=3 IsPeriodic=0
    g4: BSplineCurve PolesCount=2 KnotsCount=2 Degree=1 IsPeriodic=0
    g5: BSplineCurve PolesCount=2 KnotsCount=2 Degree=1 IsPeriodic=0
    g6: BSplineCurve PolesCount=2 KnotsCount=2 Degree=1 IsPeriodic=0
    g7: BSplineCurve PolesCount=2 KnotsCount=2 Degree=1 IsPeriodic=0
    g8: BSplineCurve PolesCount=2 KnotsCount=2 Degree=1 IsPeriodic=0
    g9: BSplineCurve PolesCount=2 KnotsCount=2 Degree=1 IsPeriodic=0
    g10: BSplineCurve PolesCount=2 KnotsCount=2 Degree=1 IsPeriodic=0
    g11: BSplineCurve PolesCount=2 KnotsCount=2 Degree=1 IsPeriodic=0
  constraints (12):
    c: Coincident(g0,g1)
    c: Coincident(g1,g2)
    c: Coincident(g2,g3)
    c: Coincident(g3,g4)
    c: Coincident(g4,g5)
    c: Coincident(g5,g6)
    c: Coincident(g6,g7)
    c: Coincident(g7,g8)
    c: Coincident(g8,g9)
    c: Coincident(g9,g10)
    c: Coincident(g10,g11)
    c: Coincident(g11,g0)
FEATURE [Sketcher::SketchObject] Sketch015  label="A"
  FullyConstrained = false
  sketch-geometry (23):
    g0: BSplineCurve PolesCount=4 KnotsCount=2 Degree=3 IsPeriodic=0
    g1: BSplineCurve PolesCount=4 KnotsCount=2 Degree=3 IsPeriodic=0
    g2: BSplineCurve PolesCount=4 KnotsCount=2 Degree=3 IsPeriodic=0
    g3: BSplineCurve PolesCount=4 KnotsCount=2 Degree=3 IsPeriodic=0
    g4: BSplineCurve PolesCount=4 KnotsCount=2 Degree=3 IsPeriodic=0
    g5: BSplineCurve PolesCount=4 KnotsCount=2 Degree=3 IsPeriodic=0
    g6: BSplineCurve PolesCount=2 KnotsCount=2 Degree=1 IsPeriodic=0
    g7: BSplineCurve PolesCount=2 KnotsCount=2 Degree=1 IsPeriodic=0
    g8: BSplineCurve PolesCount=4 KnotsCount=2 Degree=3 IsPeriodic=0
    g9: BSplineCurve PolesCount=4 KnotsCount=2 Degree=3 IsPeriodic=0
    g10: BSplineCurve PolesCount=2 KnotsCount=2 Degree=1 IsPeriodic=0
    g11: BSplineCurve PolesCount=2 KnotsCount=2 Degree=1 IsPeriodic=0
    g12: BSplineCurve PolesCount=2 KnotsCount=2 Degree=1 IsPeriodic=0
    g13: BSplineCurve PolesCount=2 KnotsCount=2 Degree=1 IsPeriodic=0
    g14: BSplineCurve PolesCount=4 KnotsCount=2 Degree=3 IsPeriodic=0
    g15: BSplineCurve PolesCount=4 KnotsCount=2 Degree=3 IsPeriodic=0
    g16: BSplineCurve PolesCount=2 KnotsCount=2 Degree=1 IsPeriodic=0
    g17: BSplineCurve PolesCount=2 KnotsCount=2 Degree=1 IsPeriodic=0
    g18: BSplineCurve PolesCount=4 KnotsCount=2 Degree=3 IsPeriodic=0
    g19: BSplineCurve PolesCount=2 KnotsCount=2 Degree=1 IsPeriodic=0
    g20: BSplineCurve PolesCount=2 KnotsCount=2 Degree=1 IsPeriodic=0
    g21: BSplineCurve PolesCount=2 KnotsCount=2 Degree=1 IsPeriodic=0
    g22: BSplineCurve PolesCount=2 KnotsCount=2 Degree=1 IsPeriodic=0
  constraints (23):
    c: Coincident(g0,g1)
    c: Coincident(g1,g2)
    c: Coincident(g2,g3)
    c: Coincident(g3,g4)
    c: Coincident(g4,g5)
    c: Coincident(g5,g6)
    c: Coincident(g6,g7)
    c: Coincident(g7,g8)
    c: Coincident(g8,g9)
    c: Coincident(g9,g10)
    c: Coincident(g10,g11)
    c: Coincident(g11,g12)
    c: Coincident(g12,g13)
    c: Coincident(g13,g14)
    c: Coincident(g14,g0)
    c: Coincident(g15,g16)
    c: Coincident(g16,g17)
    c: Coincident(g17,g18)
    c: Coincident(g18,g19)
    c: Coincident(g19,g20)
    c: Coincident(g20,g21)
    c: Coincident(g21,g22)
    c: Coincident(g22,g15)
FEATURE [Sketcher::SketchObject] Sketch016  label="S002"
  FullyConstrained = false
  sketch-geometry (26):
    g0: BSplineCurve PolesCount=4 KnotsCount=2 Degree=3 IsPeriodic=0
    g1: BSplineCurve PolesCount=4 KnotsCount=2 Degree=3 IsPeriodic=0
    g2: BSplineCurve PolesCount=4 KnotsCount=2 Degree=3 IsPeriodic=0
    g3: BSplineCurve PolesCount=4 KnotsCount=2 Degree=3 IsPeriodic=0
    g4: BSplineCurve PolesCount=4 KnotsCount=2 Degree=3 IsPeriodic=0
    g5: BSplineCurve PolesCount=4 KnotsCount=2 Degree=3 IsPeriodic=0
    g6: BSplineCurve PolesCount=4 KnotsCount=2 Degree=3 IsPeriodic=0
    g7: BSplineCurve PolesCount=4 KnotsCount=2 Degree=3 IsPeriodic=0
    g8: BSplineCurve PolesCount=4 KnotsCount=2 Degree=3 IsPeriodic=0
    g9: BSplineCurve PolesCount=4 KnotsCount=2 Degree=3 IsPeriodic=0
    g10: BSplineCurve PolesCount=4 KnotsCount=2 Degree=3 IsPeriodic=0
    g11: BSplineCurve PolesCount=4 KnotsCount=2 Degree=3 IsPeriodic=0
    g12: BSplineCurve PolesCount=4 KnotsCount=2 Degree=3 IsPeriodic=0
    g13: BSplineCurve PolesCount=4 KnotsCount=2 Degree=3 IsPeriodic=0
    g14: BSplineCurve PolesCount=4 KnotsCount=2 Degree=3 IsPeriodic=0
    g15: BSplineCurve PolesCount=2 KnotsCount=2 Degree=1 IsPeriodic=0
    g16: BSplineCurve PolesCount=2 KnotsCount=2 Degree=1 IsPeriodic=0
    g17: BSplineCurve PolesCount=4 KnotsCount=2 Degree=3 IsPeriodic=0
    g18: BSplineCurve PolesCount=4 KnotsCount=2 Degree=3 IsPeriodic=0
    g19: BSplineCurve PolesCount=4 KnotsCount=2 Degree=3 IsPeriodic=0
    g20: BSplineCurve PolesCount=4 KnotsCount=2 Degree=3 IsPeriodic=0
    g21: BSplineCurve PolesCount=4 KnotsCount=2 Degree=3 IsPeriodic=0
    g22: BSplineCurve PolesCount=4 KnotsCount=2 Degree=3 IsPeriodic=0
    g23: BSplineCurve PolesCount=4 KnotsCount=2 Degree=3 IsPeriodic=0
    g24: BSplineCurve PolesCount=4 KnotsCount=2 Degree=3 IsPeriodic=0
    g25: BSplineCurve PolesCount=2 KnotsCount=2 Degree=1 IsPeriodic=0
  constraints (26):
    c: Coincident(g0,g1)
    c: Coincident(g1,g2)
    c: Coincident(g2,g3)
    c: Coincident(g3,g4)
    c: Coincident(g4,g5)
    c: Coincident(g5,g6)
    c: Coincident(g6,g7)
    c: Coincident(g7,g8)
    c: Coincident(g8,g9)
    c: Coincident(g9,g10)
    c: Coincident(g10,g11)
    c: Coincident(g11,g12)
    c: Coincident(g12,g13)
    c: Coincident(g13,g14)
    c: Coincident(g14,g15)
    c: Coincident(g15,g16)
    c: Coincident(g16,g17)
    c: Coincident(g17,g18)
    c: Coincident(g18,g19)
    c: Coincident(g19,g20)
    c: Coincident(g20,g21)
    c: Coincident(g21,g22)
    c: Coincident(g22,g23)
    c: Coincident(g23,g24)
    c: Coincident(g24,g25)
    c: Coincident(g25,g0)
FEATURE [Sketcher::SketchObject] Sketch017  label="House"
  FullyConstrained = false
  MapMode = 5
  Support = -> [XY_Plane]
  sketch-geometry (422):
    g0: BSplineCurve PolesCount=4 KnotsCount=2 Degree=3 IsPeriodic=0
    g1: BSplineCurve PolesCount=4 KnotsCount=2 Degree=3 IsPeriodic=0
    g2: BSplineCurve PolesCount=2 KnotsCount=2 Degree=1 IsPeriodic=0
    g3: BSplineCurve PolesCount=2 KnotsCount=2 Degree=1 IsPeriodic=0
    g4: BSplineCurve PolesCount=2 KnotsCount=2 Degree=1 IsPeriodic=0
    g5: BSplineCurve PolesCount=2 KnotsCount=2 Degree=1 IsPeriodic=0
    g6: BSplineCurve PolesCount=4 KnotsCount=2 Degree=3 IsPeriodic=0
    g7: BSplineCurve PolesCount=2 KnotsCount=2 Degree=1 IsPeriodic=0
    g8: BSplineCurve PolesCount=2 KnotsCount=2 Degree=1 IsPeriodic=0
    g9: BSplineCurve PolesCount=2 KnotsCount=2 Degree=1 IsPeriodic=0
    g10: BSplineCurve PolesCount=2 KnotsCount=2 Degree=1 IsPeriodic=0
    g11: BSplineCurve PolesCount=4 KnotsCount=2 Degree=3 IsPeriodic=0
    g12: BSplineCurve PolesCount=4 KnotsCount=2 Degree=3 IsPeriodic=0
    g13: BSplineCurve PolesCount=4 KnotsCount=2 Degree=3 IsPeriodic=0
    g14: BSplineCurve PolesCount=2 KnotsCount=2 Degree=1 IsPeriodic=0
    g15: BSplineCurve PolesCount=2 KnotsCount=2 Degree=1 IsPeriodic=0
    g16: BSplineCurve PolesCount=4 KnotsCount=2 Degree=3 IsPeriodic=0
    g17: BSplineCurve PolesCount=2 KnotsCount=2 Degree=1 IsPeriodic=0
    g18: BSplineCurve PolesCount=2 KnotsCount=2 Degree=1 IsPeriodic=0
    g19: BSplineCurve PolesCount=4 KnotsCount=2 Degree=3 IsPeriodic=0
    g20: BSplineCurve PolesCount=4 KnotsCount=2 Degree=3 IsPeriodic=0
    g21: BSplineCurve PolesCount=4 KnotsCount=2 Degree=3 IsPeriodic=0
    g22: BSplineCurve PolesCount=4 KnotsCount=2 Degree=3 IsPeriodic=0
    g23: BSplineCurve PolesCount=4 KnotsCount=2 Degree=3 IsPeriodic=0
    g24: BSplineCurve PolesCount=4 KnotsCount=2 Degree=3 IsPeriodic=0
    g25: BSplineCurve PolesCount=2 KnotsCount=2 Degree=1 IsPeriodic=0
    g26: BSplineCurve PolesCount=2 KnotsCount=2 Degree=1 IsPeriodic=0
    g27: BSplineCurve PolesCount=4 KnotsCount=2 Degree=3 IsPeriodic=0
    g28: BSplineCurve PolesCount=4 KnotsCount=2 Degree=3 IsPeriodic=0
    g29: BSplineCurve PolesCount=4 KnotsCount=2 Degree=3 IsPeriodic=0
    g30: BSplineCurve PolesCount=4 KnotsCount=2 Degree=3 IsPeriodic=0
    g31: BSplineCurve PolesCount=4 KnotsCount=2 Degree=3 IsPeriodic=0
    g32: BSplineCurve PolesCount=2 KnotsCount=2 Degree=1 IsPeriodic=0
    g33: BSplineCurve PolesCount=2 KnotsCount=2 Degree=1 IsPeriodic=0
    g34: BSplineCurve PolesCount=4 KnotsCount=2 Degree=3 IsPeriodic=0
    g35: BSplineCurve PolesCount=4 KnotsCount=2 Degree=3 IsPeriodic=0
    g36: BSplineCurve PolesCount=4 KnotsCount=2 Degree=3 IsPeriodic=0
    g37: BSplineCurve PolesCount=4 KnotsCount=2 Degree=3 IsPeriodic=0
    g38: BSplineCurve PolesCount=4 KnotsCount=2 Degree=3 IsPeriodic=0
    g39: BSplineCurve PolesCount=2 KnotsCount=2 Degree=1 IsPeriodic=0
    g40: BSplineCurve PolesCount=2 KnotsCount=2 Degree=1 IsPeriodic=0
    g41: BSplineCurve PolesCount=4 KnotsCount=2 Degree=3 IsPeriodic=0
    g42: BSplineCurve PolesCount=4 KnotsCount=2 Degree=3 IsPeriodic=0
    g43: BSplineCurve PolesCount=4 KnotsCount=2 Degree=3 IsPeriodic=0
    g44: BSplineCurve PolesCount=4 KnotsCount=2 Degree=3 IsPeriodic=0
    g45: BSplineCurve PolesCount=4 KnotsCount=2 Degree=3 IsPeriodic=0
    g46: BSplineCurve PolesCount=4 KnotsCount=2 Degree=3 IsPeriodic=0
    g47: BSplineCurve PolesCount=4 KnotsCount=2 Degree=3 IsPeriodic=0
    g48: BSplineCurve PolesCount=4 KnotsCount=2 Degree=3 IsPeriodic=0
    g49: BSplineCurve PolesCount=4 KnotsCount=2 Degree=3 IsPeriodic=0
    g50: BSplineCurve PolesCount=4 KnotsCount=2 Degree=3 IsPeriodic=0
    g51: BSplineCurve PolesCount=4 KnotsCount=2 Degree=3 IsPeriodic=0
    g52: BSplineCurve PolesCount=4 KnotsCount=2 Degree=3 IsPeriodic=0
    g53: BSplineCurve PolesCount=4 KnotsCount=2 Degree=3 IsPeriodic=0
    g54: BSplineCurve PolesCount=4 KnotsCount=2 Degree=3 IsPeriodic=0
    g55: BSplineCurve PolesCount=4 KnotsCount=2 Degree=3 IsPeriodic=0
    g56: BSplineCurve PolesCount=4 KnotsCount=2 Degree=3 IsPeriodic=0
    g57: BSplineCurve PolesCount=2 KnotsCount=2 Degree=1 IsPeriodic=0
    g58: BSplineCurve PolesCount=2 KnotsCount=2 Degree=1 IsPeriodic=0
    g59: BSplineCurve PolesCount=4 KnotsCount=2 Degree=3 IsPeriodic=0
    g60: BSplineCurve PolesCount=4 KnotsCount=2 Degree=3 IsPeriodic=0
    g61: BSplineCurve PolesCount=4 KnotsCount=2 Degree=3 IsPeriodic=0
    g62: BSplineCurve PolesCount=4 KnotsCount=2 Degree=3 IsPeriodic=0
    g63: BSplineCurve PolesCount=4 KnotsCount=2 Degree=3 IsPeriodic=0
    g64: BSplineCurve PolesCount=4 KnotsCount=2 Degree=3 IsPeriodic=0
    g65: BSplineCurve PolesCount=4 KnotsCount=2 Degree=3 IsPeriodic=0
    g66: BSplineCurve PolesCount=4 KnotsCount=2 Degree=3 IsPeriodic=0
    g67: BSplineCurve PolesCount=4 KnotsCount=2 Degree=3 IsPeriodic=0
    g68: BSplineCurve PolesCount=2 KnotsCount=2 Degree=1 IsPeriodic=0
    g69: BSplineCurve PolesCount=2 KnotsCount=2 Degree=1 IsPeriodic=0
    g70: BSplineCurve PolesCount=4 KnotsCount=2 Degree=3 IsPeriodic=0
    g71: BSplineCurve PolesCount=4 KnotsCount=2 Degree=3 IsPeriodic=0
    g72: BSplineCurve PolesCount=4 KnotsCount=2 Degree=3 IsPeriodic=0
    g73: BSplineCurve PolesCount=4 KnotsCount=2 Degree=3 IsPeriodic=0
    g74: BSplineCurve PolesCount=4 KnotsCount=2 Degree=3 IsPeriodic=0
    g75: BSplineCurve PolesCount=4 KnotsCount=2 Degree=3 IsPeriodic=0
    g76: BSplineCurve PolesCount=4 KnotsCount=2 Degree=3 IsPeriodic=0
    g77: BSplineCurve PolesCount=4 KnotsCount=2 Degree=3 IsPeriodic=0
    g78: BSplineCurve PolesCount=4 KnotsCount=2 Degree=3 IsPeriodic=0
    g79: BSplineCurve PolesCount=4 KnotsCount=2 Degree=3 IsPeriodic=0
    g80: BSplineCurve PolesCount=4 KnotsCount=2 Degree=3 IsPeriodic=0
    g81: BSplineCurve PolesCount=2 KnotsCount=2 Degree=1 IsPeriodic=0
    g82: BSplineCurve PolesCount=2 KnotsCount=2 Degree=1 IsPeriodic=0
    g83: BSplineCurve PolesCount=2 KnotsCount=2 Degree=1 IsPeriodic=0
    g84: BSplineCurve PolesCount=2 KnotsCount=2 Degree=1 IsPeriodic=0
    g85: BSplineCurve PolesCount=2 KnotsCount=2 Degree=1 IsPeriodic=0
    g86: BSplineCurve PolesCount=2 KnotsCount=2 Degree=1 IsPeriodic=0
    g87: BSplineCurve PolesCount=4 KnotsCount=2 Degree=3 IsPeriodic=0
    g88: BSplineCurve PolesCount=4 KnotsCount=2 Degree=3 IsPeriodic=0
    g89: BSplineCurve PolesCount=2 KnotsCount=2 Degree=1 IsPeriodic=0
    g90: BSplineCurve PolesCount=2 KnotsCount=2 Degree=1 IsPeriodic=0
    g91: BSplineCurve PolesCount=2 KnotsCount=2 Degree=1 IsPeriodic=0
    g92: BSplineCurve PolesCount=2 KnotsCount=2 Degree=1 IsPeriodic=0
    g93: BSplineCurve PolesCount=4 KnotsCount=2 Degree=3 IsPeriodic=0
    g94: BSplineCurve PolesCount=2 KnotsCount=2 Degree=1 IsPeriodic=0
    g95: BSplineCurve PolesCount=2 KnotsCount=2 Degree=1 IsPeriodic=0
    g96: BSplineCurve PolesCount=2 KnotsCount=2 Degree=1 IsPeriodic=0
    g97: BSplineCurve PolesCount=2 KnotsCount=2 Degree=1 IsPeriodic=0
    g98: BSplineCurve PolesCount=4 KnotsCount=2 Degree=3 IsPeriodic=0
    g99: BSplineCurve PolesCount=4 KnotsCount=2 Degree=3 IsPeriodic=0
    g100: BSplineCurve PolesCount=4 KnotsCount=2 Degree=3 IsPeriodic=0
    g101: BSplineCurve PolesCount=4 KnotsCount=2 Degree=3 IsPeriodic=0
    g102: BSplineCurve PolesCount=4 KnotsCount=2 Degree=3 IsPeriodic=0
    g103: BSplineCurve PolesCount=2 KnotsCount=2 Degree=1 IsPeriodic=0
    g104: BSplineCurve PolesCount=2 KnotsCount=2 Degree=1 IsPeriodic=0
    g105: BSplineCurve PolesCount=2 KnotsCount=2 Degree=1 IsPeriodic=0
    g106: BSplineCurve PolesCount=2 KnotsCount=2 Degree=1 IsPeriodic=0
    g107: BSplineCurve PolesCount=4 KnotsCount=2 Degree=3 IsPeriodic=0
    g108: BSplineCurve PolesCount=4 KnotsCount=2 Degree=3 IsPeriodic=0
    g109: BSplineCurve PolesCount=4 KnotsCount=2 Degree=3 IsPeriodic=0
    g110: BSplineCurve PolesCount=4 KnotsCount=2 Degree=3 IsPeriodic=0
    g111: BSplineCurve PolesCount=4 KnotsCount=2 Degree=3 IsPeriodic=0
    g112: BSplineCurve PolesCount=4 KnotsCount=2 Degree=3 IsPeriodic=0
    g113: BSplineCurve PolesCount=4 KnotsCount=2 Degree=3 IsPeriodic=0
    g114: BSplineCurve PolesCount=4 KnotsCount=2 Degree=3 IsPeriodic=0
    g115: BSplineCurve PolesCount=4 KnotsCount=2 Degree=3 IsPeriodic=0
    g116: BSplineCurve PolesCount=4 KnotsCount=2 Degree=3 IsPeriodic=0
    g117: BSplineCurve PolesCount=4 KnotsCount=2 Degree=3 IsPeriodic=0
    g118: BSplineCurve PolesCount=2 KnotsCount=2 Degree=1 IsPeriodic=0
    g119: BSplineCurve PolesCount=2 KnotsCount=2 Degree=1 IsPeriodic=0
    g120: BSplineCurve PolesCount=4 KnotsCount=2 Degree=3 IsPeriodic=0
    g121: BSplineCurve PolesCount=4 KnotsCount=2 Degree=3 IsPeriodic=0
    g122: BSplineCurve PolesCount=4 KnotsCount=2 Degree=3 IsPeriodic=0
    g123: BSplineCurve PolesCount=4 KnotsCount=2 Degree=3 IsPeriodic=0
    g124: BSplineCurve PolesCount=2 KnotsCount=2 Degree=1 IsPeriodic=0
    g125: BSplineCurve PolesCount=2 KnotsCount=2 Degree=1 IsPeriodic=0
    g126: BSplineCurve PolesCount=2 KnotsCount=2 Degree=1 IsPeriodic=0
    g127: BSplineCurve PolesCount=2 KnotsCount=2 Degree=1 IsPeriodic=0
    g128: BSplineCurve PolesCount=2 KnotsCount=2 Degree=1 IsPeriodic=0
    g129: BSplineCurve PolesCount=2 KnotsCount=2 Degree=1 IsPeriodic=0
    g130: BSplineCurve PolesCount=2 KnotsCount=2 Degree=1 IsPeriodic=0
    g131: BSplineCurve PolesCount=2 KnotsCount=2 Degree=1 IsPeriodic=0
    g132: BSplineCurve PolesCount=2 KnotsCount=2 Degree=1 IsPeriodic=0
    g133: BSplineCurve PolesCount=2 KnotsCount=2 Degree=1 IsPeriodic=0
    g134: BSplineCurve PolesCount=4 KnotsCount=2 Degree=3 IsPeriodic=0
    g135: BSplineCurve PolesCount=4 KnotsCount=2 Degree=3 IsPeriodic=0
    g136: BSplineCurve PolesCount=2 KnotsCount=2 Degree=1 IsPeriodic=0
    g137: BSplineCurve PolesCount=2 KnotsCount=2 Degree=1 IsPeriodic=0
    g138: BSplineCurve PolesCount=2 KnotsCount=2 Degree=1 IsPeriodic=0
    g139: BSplineCurve PolesCount=2 KnotsCount=2 Degree=1 IsPeriodic=0
    g140: BSplineCurve PolesCount=4 KnotsCount=2 Degree=3 IsPeriodic=0
    g141: BSplineCurve PolesCount=4 KnotsCount=2 Degree=3 IsPeriodic=0
    g142: BSplineCurve PolesCount=4 KnotsCount=2 Degree=3 IsPeriodic=0
    g143: BSplineCurve PolesCount=4 KnotsCount=2 Degree=3 IsPeriodic=0
    g144: BSplineCurve PolesCount=4 KnotsCount=2 Degree=3 IsPeriodic=0
    g145: BSplineCurve PolesCount=4 KnotsCount=2 Degree=3 IsPeriodic=0
    g146: BSplineCurve PolesCount=4 KnotsCount=2 Degree=3 IsPeriodic=0
    g147: BSplineCurve PolesCount=4 KnotsCount=2 Degree=3 IsPeriodic=0
    g148: BSplineCurve PolesCount=4 KnotsCount=2 Degree=3 IsPeriodic=0
    g149: BSplineCurve PolesCount=4 KnotsCount=2 Degree=3 IsPeriodic=0
    g150: BSplineCurve PolesCount=4 KnotsCount=2 Degree=3 IsPeriodic=0
    g151: BSplineCurve PolesCount=4 KnotsCount=2 Degree=3 IsPeriodic=0
    g152: BSplineCurve PolesCount=4 KnotsCount=2 Degree=3 IsPeriodic=0
    g153: BSplineCurve PolesCount=4 KnotsCount=2 Degree=3 IsPeriodic=0
    g154: BSplineCurve PolesCount=4 KnotsCount=2 Degree=3 IsPeriodic=0
    g155: BSplineCurve PolesCount=4 KnotsCount=2 Degree=3 IsPeriodic=0
    g156: BSplineCurve PolesCount=4 KnotsCount=2 Degree=3 IsPeriodic=0
    g157: BSplineCurve PolesCount=4 KnotsCount=2 Degree=3 IsPeriodic=0
    g158: BSplineCurve PolesCount=2 KnotsCount=2 Degree=1 IsPeriodic=0
    g159: BSplineCurve PolesCount=2 KnotsCount=2 Degree=1 IsPeriodic=0
    g160: BSplineCurve PolesCount=4 KnotsCount=2 Degree=3 IsPeriodic=0
    g161: BSplineCurve PolesCount=4 KnotsCount=2 Degree=3 IsPeriodic=0
    g162: BSplineCurve PolesCount=4 KnotsCount=2 Degree=3 IsPeriodic=0
    g163: BSplineCurve PolesCount=4 KnotsCount=2 Degree=3 IsPeriodic=0
    g164: BSplineCurve PolesCount=4 KnotsCount=2 Degree=3 IsPeriodic=0
    g165: BSplineCurve PolesCount=2 KnotsCount=2 Degree=1 IsPeriodic=0
    g166: BSplineCurve PolesCount=2 KnotsCount=2 Degree=1 IsPeriodic=0
    g167: BSplineCurve PolesCount=4 KnotsCount=2 Degree=3 IsPeriodic=0
    g168: BSplineCurve PolesCount=4 KnotsCount=2 Degree=3 IsPeriodic=0
    g169: BSplineCurve PolesCount=4 KnotsCount=2 Degree=3 IsPeriodic=0
    g170: BSplineCurve PolesCount=4 KnotsCount=2 Degree=3 IsPeriodic=0
    g171: BSplineCurve PolesCount=4 KnotsCount=2 Degree=3 IsPeriodic=0
    g172: BSplineCurve PolesCount=2 KnotsCount=2 Degree=1 IsPeriodic=0
    g173: BSplineCurve PolesCount=2 KnotsCount=2 Degree=1 IsPeriodic=0
    g174: BSplineCurve PolesCount=4 KnotsCount=2 Degree=3 IsPeriodic=0
    g175: BSplineCurve PolesCount=4 KnotsCount=2 Degree=3 IsPeriodic=0
    g176: BSplineCurve PolesCount=4 KnotsCount=2 Degree=3 IsPeriodic=0
    g177: BSplineCurve PolesCount=4 KnotsCount=2 Degree=3 IsPeriodic=0
    g178: BSplineCurve PolesCount=4 KnotsCount=2 Degree=3 IsPeriodic=0
    g179: BSplineCurve PolesCount=4 KnotsCount=2 Degree=3 IsPeriodic=0
    g180: BSplineCurve PolesCount=4 KnotsCount=2 Degree=3 IsPeriodic=0
    g181: BSplineCurve PolesCount=2 KnotsCount=2 Degree=1 IsPeriodic=0
    g182: BSplineCurve PolesCount=2 KnotsCount=2 Degree=1 IsPeriodic=0
    g183: BSplineCurve PolesCount=4 KnotsCount=2 Degree=3 IsPeriodic=0
    g184: BSplineCurve PolesCount=4 KnotsCount=2 Degree=3 IsPeriodic=0
    g185: BSplineCurve PolesCount=2 KnotsCount=2 Degree=1 IsPeriodic=0
    g186: BSplineCurve PolesCount=2 KnotsCount=2 Degree=1 IsPeriodic=0
    g187: BSplineCurve PolesCount=2 KnotsCount=2 Degree=1 IsPeriodic=0
    g188: BSplineCurve PolesCount=2 KnotsCount=2 Degree=1 IsPeriodic=0
    g189: BSplineCurve PolesCount=4 KnotsCount=2 Degree=3 IsPeriodic=0
    g190: BSplineCurve PolesCount=2 KnotsCount=2 Degree=1 IsPeriodic=0
    g191: BSplineCurve PolesCount=2 KnotsCount=2 Degree=1 IsPeriodic=0
    g192: BSplineCurve PolesCount=2 KnotsCount=2 Degree=1 IsPeriodic=0
    g193: BSplineCurve PolesCount=2 KnotsCount=2 Degree=1 IsPeriodic=0
    g194: BSplineCurve PolesCount=2 KnotsCount=2 Degree=1 IsPeriodic=0
    g195: BSplineCurve PolesCount=4 KnotsCount=2 Degree=3 IsPeriodic=0
    g196: BSplineCurve PolesCount=4 KnotsCount=2 Degree=3 IsPeriodic=0
    g197: BSplineCurve PolesCount=4 KnotsCount=2 Degree=3 IsPeriodic=0
    g198: BSplineCurve PolesCount=4 KnotsCount=2 Degree=3 IsPeriodic=0
    g199: BSplineCurve PolesCount=4 KnotsCount=2 Degree=3 IsPeriodic=0
    g200: BSplineCurve PolesCount=4 KnotsCount=2 Degree=3 IsPeriodic=0
    g201: BSplineCurve PolesCount=4 KnotsCount=2 Degree=3 IsPeriodic=0
    g202: BSplineCurve PolesCount=4 KnotsCount=2 Degree=3 IsPeriodic=0
    g203: BSplineCurve PolesCount=4 KnotsCount=2 Degree=3 IsPeriodic=0
    g204: BSplineCurve PolesCount=2 KnotsCount=2 Degree=1 IsPeriodic=0
    g205: BSplineCurve PolesCount=2 KnotsCount=2 Degree=1 IsPeriodic=0
    g206: BSplineCurve PolesCount=2 KnotsCount=2 Degree=1 IsPeriodic=0
    g207: BSplineCurve PolesCount=2 KnotsCount=2 Degree=1 IsPeriodic=0
    g208: BSplineCurve PolesCount=4 KnotsCount=2 Degree=3 IsPeriodic=0
    g209: BSplineCurve PolesCount=4 KnotsCount=2 Degree=3 IsPeriodic=0
    g210: BSplineCurve PolesCount=2 KnotsCount=2 Degree=1 IsPeriodic=0
    g211: BSplineCurve PolesCount=2 KnotsCount=2 Degree=1 IsPeriodic=0
    g212: BSplineCurve PolesCount=4 KnotsCount=2 Degree=3 IsPeriodic=0
    g213: BSplineCurve PolesCount=2 KnotsCount=2 Degree=1 IsPeriodic=0
    g214: BSplineCurve PolesCount=2 KnotsCount=2 Degree=1 IsPeriodic=0
    g215: BSplineCurve PolesCount=4 KnotsCount=2 Degree=3 IsPeriodic=0
    g216: BSplineCurve PolesCount=4 KnotsCount=2 Degree=3 IsPeriodic=0
    g217: BSplineCurve PolesCount=4 KnotsCount=2 Degree=3 IsPeriodic=0
    g218: BSplineCurve PolesCount=4 KnotsCount=2 Degree=3 IsPeriodic=0
    g219: BSplineCurve PolesCount=4 KnotsCount=2 Degree=3 IsPeriodic=0
    g220: BSplineCurve PolesCount=4 KnotsCount=2 Degree=3 IsPeriodic=0
    g221: BSplineCurve PolesCount=4 KnotsCount=2 Degree=3 IsPeriodic=0
    g222: BSplineCurve PolesCount=4 KnotsCount=2 Degree=3 IsPeriodic=0
    g223: BSplineCurve PolesCount=4 KnotsCount=2 Degree=3 IsPeriodic=0
    g224: BSplineCurve PolesCount=4 KnotsCount=2 Degree=3 IsPeriodic=0
    g225: BSplineCurve PolesCount=4 KnotsCount=2 Degree=3 IsPeriodic=0
    g226: BSplineCurve PolesCount=4 KnotsCount=2 Degree=3 IsPeriodic=0
    g227: BSplineCurve PolesCount=4 KnotsCount=2 Degree=3 IsPeriodic=0
    g228: BSplineCurve PolesCount=4 KnotsCount=2 Degree=3 IsPeriodic=0
    g229: BSplineCurve PolesCount=4 KnotsCount=2 Degree=3 IsPeriodic=0
    g230: BSplineCurve PolesCount=4 KnotsCount=2 Degree=3 IsPeriodic=0
    g231: BSplineCurve PolesCount=4 KnotsCount=2 Degree=3 IsPeriodic=0
    g232: BSplineCurve PolesCount=4 KnotsCount=2 Degree=3 IsPeriodic=0
    g233: BSplineCurve PolesCount=4 KnotsCount=2 Degree=3 IsPeriodic=0
    g234: BSplineCurve PolesCount=2 KnotsCount=2 Degree=1 IsPeriodic=0
    g235: BSplineCurve PolesCount=2 KnotsCount=2 Degree=1 IsPeriodic=0
    g236: BSplineCurve PolesCount=4 KnotsCount=2 Degree=3 IsPeriodic=0
    g237: BSplineCurve PolesCount=4 KnotsCount=2 Degree=3 IsPeriodic=0
    g238: BSplineCurve PolesCount=2 KnotsCount=2 Degree=1 IsPeriodic=0
    g239: BSplineCurve PolesCount=4 KnotsCount=2 Degree=3 IsPeriodic=0
    g240: BSplineCurve PolesCount=4 KnotsCount=2 Degree=3 IsPeriodic=0
    g241: BSplineCurve PolesCount=4 KnotsCount=2 Degree=3 IsPeriodic=0
    g242: BSplineCurve PolesCount=4 KnotsCount=2 Degree=3 IsPeriodic=0
    g243: BSplineCurve PolesCount=4 KnotsCount=2 Degree=3 IsPeriodic=0
    g244: BSplineCurve PolesCount=4 KnotsCount=2 Degree=3 IsPeriodic=0
    g245: BSplineCurve PolesCount=2 KnotsCount=2 Degree=1 IsPeriodic=0
    g246: BSplineCurve PolesCount=2 KnotsCount=2 Degree=1 IsPeriodic=0
    g247: BSplineCurve PolesCount=4 KnotsCount=2 Degree=3 IsPeriodic=0
    g248: BSplineCurve PolesCount=4 KnotsCount=2 Degree=3 IsPeriodic=0
    g249: BSplineCurve PolesCount=4 KnotsCount=2 Degree=3 IsPeriodic=0
    g250: BSplineCurve PolesCount=4 KnotsCount=2 Degree=3 IsPeriodic=0
    g251: BSplineCurve PolesCount=4 KnotsCount=2 Degree=3 IsPeriodic=0
    g252: BSplineCurve PolesCount=2 KnotsCount=2 Degree=1 IsPeriodic=0
    g253: BSplineCurve PolesCount=4 KnotsCount=2 Degree=3 IsPeriodic=0
    g254: BSplineCurve PolesCount=4 KnotsCount=2 Degree=3 IsPeriodic=0
    g255: BSplineCurve PolesCount=4 KnotsCount=2 Degree=3 IsPeriodic=0
    g256: BSplineCurve PolesCount=4 KnotsCount=2 Degree=3 IsPeriodic=0
    g257: BSplineCurve PolesCount=2 KnotsCount=2 Degree=1 IsPeriodic=0
    g258: BSplineCurve PolesCount=2 KnotsCount=2 Degree=1 IsPeriodic=0
    g259: BSplineCurve PolesCount=4 KnotsCount=2 Degree=3 IsPeriodic=0
    g260: BSplineCurve PolesCount=4 KnotsCount=2 Degree=3 IsPeriodic=0
    g261: BSplineCurve PolesCount=4 KnotsCount=2 Degree=3 IsPeriodic=0
    g262: BSplineCurve PolesCount=4 KnotsCount=2 Degree=3 IsPeriodic=0
    g263: BSplineCurve PolesCount=4 KnotsCount=2 Degree=3 IsPeriodic=0
    g264: BSplineCurve PolesCount=4 KnotsCount=2 Degree=3 IsPeriodic=0
    g265: BSplineCurve PolesCount=4 KnotsCount=2 Degree=3 IsPeriodic=0
    g266: BSplineCurve PolesCount=4 KnotsCount=2 Degree=3 IsPeriodic=0
    g267: BSplineCurve PolesCount=4 KnotsCount=2 Degree=3 IsPeriodic=0
    g268: BSplineCurve PolesCount=4 KnotsCount=2 Degree=3 IsPeriodic=0
    g269: BSplineCurve PolesCount=4 KnotsCount=2 Degree=3 IsPeriodic=0
    g270: BSplineCurve PolesCount=4 KnotsCount=2 Degree=3 IsPeriodic=0
    g271: BSplineCurve PolesCount=4 KnotsCount=2 Degree=3 IsPeriodic=0
    g272: BSplineCurve PolesCount=4 KnotsCount=2 Degree=3 IsPeriodic=0
    g273: BSplineCurve PolesCount=4 KnotsCount=2 Degree=3 IsPeriodic=0
    g274: BSplineCurve PolesCount=4 KnotsCount=2 Degree=3 IsPeriodic=0
    g275: BSplineCurve PolesCount=4 KnotsCount=2 Degree=3 IsPeriodic=0
    g276: BSplineCurve PolesCount=4 KnotsCount=2 Degree=3 IsPeriodic=0
    g277: BSplineCurve PolesCount=4 KnotsCount=2 Degree=3 IsPeriodic=0
    g278: BSplineCurve PolesCount=4 KnotsCount=2 Degree=3 IsPeriodic=0
    g279: BSplineCurve PolesCount=4 KnotsCount=2 Degree=3 IsPeriodic=0
    g280: BSplineCurve PolesCount=4 KnotsCount=2 Degree=3 IsPeriodic=0
    g281: BSplineCurve PolesCount=4 KnotsCount=2 Degree=3 IsPeriodic=0
    g282: BSplineCurve PolesCount=4 KnotsCount=2 Degree=3 IsPeriodic=0
    g283: BSplineCurve PolesCount=4 KnotsCount=2 Degree=3 IsPeriodic=0
    g284: BSplineCurve PolesCount=4 KnotsCount=2 Degree=3 IsPeriodic=0
    g285: BSplineCurve PolesCount=4 KnotsCount=2 Degree=3 IsPeriodic=0
    g286: BSplineCurve PolesCount=4 KnotsCount=2 Degree=3 IsPeriodic=0
    g287: BSplineCurve PolesCount=4 KnotsCount=2 Degree=3 IsPeriodic=0
    g288: BSplineCurve PolesCount=4 KnotsCount=2 Degree=3 IsPeriodic=0
    g289: BSplineCurve PolesCount=4 KnotsCount=2 Degree=3 IsPeriodic=0
    g290: BSplineCurve PolesCount=4 KnotsCount=2 Degree=3 IsPeriodic=0
    g291: BSplineCurve PolesCount=4 KnotsCount=2 Degree=3 IsPeriodic=0
    g292: BSplineCurve PolesCount=4 KnotsCount=2 Degree=3 IsPeriodic=0
    g293: BSplineCurve PolesCount=4 KnotsCount=2 Degree=3 IsPeriodic=0
    g294: BSplineCurve PolesCount=4 KnotsCount=2 Degree=3 IsPeriodic=0
    g295: BSplineCurve PolesCount=4 KnotsCount=2 Degree=3 IsPeriodic=0
    g296: BSplineCurve PolesCount=4 KnotsCount=2 Degree=3 IsPeriodic=0
    g297: BSplineCurve PolesCount=4 KnotsCount=2 Degree=3 IsPeriodic=0
    g298: BSplineCurve PolesCount=4 KnotsCount=2 Degree=3 IsPeriodic=0
    g299: BSplineCurve PolesCount=4 KnotsCount=2 Degree=3 IsPeriodic=0
    g300: BSplineCurve PolesCount=4 KnotsCount=2 Degree=3 IsPeriodic=0
    g301: BSplineCurve PolesCount=4 KnotsCount=2 Degree=3 IsPeriodic=0
    g302: BSplineCurve PolesCount=4 KnotsCount=2 Degree=3 IsPeriodic=0
    g303: BSplineCurve PolesCount=4 KnotsCount=2 Degree=3 IsPeriodic=0
    g304: BSplineCurve PolesCount=2 KnotsCount=2 Degree=1 IsPeriodic=0
    g305: BSplineCurve PolesCount=2 KnotsCount=2 Degree=1 IsPeriodic=0
    g306: BSplineCurve PolesCount=4 KnotsCount=2 Degree=3 IsPeriodic=0
    g307: BSplineCurve PolesCount=4 KnotsCount=2 Degree=3 IsPeriodic=0
    g308: BSplineCurve PolesCount=2 KnotsCount=2 Degree=1 IsPeriodic=0
    g309: BSplineCurve PolesCount=4 KnotsCount=2 Degree=3 IsPeriodic=0
    g310: BSplineCurve PolesCount=4 KnotsCount=2 Degree=3 IsPeriodic=0
    g311: BSplineCurve PolesCount=4 KnotsCount=2 Degree=3 IsPeriodic=0
    g312: BSplineCurve PolesCount=4 KnotsCount=2 Degree=3 IsPeriodic=0
    g313: BSplineCurve PolesCount=4 KnotsCount=2 Degree=3 IsPeriodic=0
    g314: BSplineCurve PolesCount=4 KnotsCount=2 Degree=3 IsPeriodic=0
    g315: BSplineCurve PolesCount=4 KnotsCount=2 Degree=3 IsPeriodic=0
    g316: BSplineCurve PolesCount=4 KnotsCount=2 Degree=3 IsPeriodic=0
    g317: BSplineCurve PolesCount=4 KnotsCount=2 Degree=3 IsPeriodic=0
    g318: BSplineCurve PolesCount=2 KnotsCount=2 Degree=1 IsPeriodic=0
    g319: BSplineCurve PolesCount=2 KnotsCount=2 Degree=1 IsPeriodic=0
    g320: BSplineCurve PolesCount=4 KnotsCount=2 Degree=3 IsPeriodic=0
    g321: BSplineCurve PolesCount=4 KnotsCount=2 Degree=3 IsPeriodic=0
    g322: BSplineCurve PolesCount=4 KnotsCount=2 Degree=3 IsPeriodic=0
    g323: BSplineCurve PolesCount=4 KnotsCount=2 Degree=3 IsPeriodic=0
    g324: BSplineCurve PolesCount=4 KnotsCount=2 Degree=3 IsPeriodic=0
    g325: BSplineCurve PolesCount=4 KnotsCount=2 Degree=3 IsPeriodic=0
    g326: BSplineCurve PolesCount=4 KnotsCount=2 Degree=3 IsPeriodic=0
    g327: BSplineCurve PolesCount=4 KnotsCount=2 Degree=3 IsPeriodic=0
    g328: BSplineCurve PolesCount=4 KnotsCount=2 Degree=3 IsPeriodic=0
    g329: BSplineCurve PolesCount=4 KnotsCount=2 Degree=3 IsPeriodic=0
    g330: BSplineCurve PolesCount=4 KnotsCount=2 Degree=3 IsPeriodic=0
    g331: BSplineCurve PolesCount=4 KnotsCount=2 Degree=3 IsPeriodic=0
    g332: BSplineCurve PolesCount=4 KnotsCount=2 Degree=3 IsPeriodic=0
    g333: BSplineCurve PolesCount=4 KnotsCount=2 Degree=3 IsPeriodic=0
    g334: BSplineCurve PolesCount=4 KnotsCount=2 Degree=3 IsPeriodic=0
    g335: BSplineCurve PolesCount=4 KnotsCount=2 Degree=3 IsPeriodic=0
    g336: BSplineCurve PolesCount=2 KnotsCount=2 Degree=1 IsPeriodic=0
    g337: BSplineCurve PolesCount=4 KnotsCount=2 Degree=3 IsPeriodic=0
    g338: BSplineCurve PolesCount=4 KnotsCount=2 Degree=3 IsPeriodic=0
    g339: BSplineCurve PolesCount=4 KnotsCount=2 Degree=3 IsPeriodic=0
    g340: BSplineCurve PolesCount=4 KnotsCount=2 Degree=3 IsPeriodic=0
    g341: BSplineCurve PolesCount=4 KnotsCount=2 Degree=3 IsPeriodic=0
    g342: BSplineCurve PolesCount=2 KnotsCount=2 Degree=1 IsPeriodic=0
    g343: BSplineCurve PolesCount=2 KnotsCount=2 Degree=1 IsPeriodic=0
    g344: BSplineCurve PolesCount=4 KnotsCount=2 Degree=3 IsPeriodic=0
    g345: BSplineCurve PolesCount=4 KnotsCount=2 Degree=3 IsPeriodic=0
    g346: BSplineCurve PolesCount=4 KnotsCount=2 Degree=3 IsPeriodic=0
    g347: BSplineCurve PolesCount=4 KnotsCount=2 Degree=3 IsPeriodic=0
    g348: BSplineCurve PolesCount=4 KnotsCount=2 Degree=3 IsPeriodic=0
    g349: BSplineCurve PolesCount=4 KnotsCount=2 Degree=3 IsPeriodic=0
    g350: BSplineCurve PolesCount=4 KnotsCount=2 Degree=3 IsPeriodic=0
    g351: BSplineCurve PolesCount=4 KnotsCount=2 Degree=3 IsPeriodic=0
    g352: BSplineCurve PolesCount=4 KnotsCount=2 Degree=3 IsPeriodic=0
    g353: BSplineCurve PolesCount=4 KnotsCount=2 Degree=3 IsPeriodic=0
    g354: BSplineCurve PolesCount=4 KnotsCount=2 Degree=3 IsPeriodic=0
    g355: BSplineCurve PolesCount=4 KnotsCount=2 Degree=3 IsPeriodic=0
    g356: BSplineCurve PolesCount=4 KnotsCount=2 Degree=3 IsPeriodic=0
    g357: BSplineCurve PolesCount=4 KnotsCount=2 Degree=3 IsPeriodic=0
    g358: BSplineCurve PolesCount=4 KnotsCount=2 Degree=3 IsPeriodic=0
    g359: BSplineCurve PolesCount=4 KnotsCount=2 Degree=3 IsPeriodic=0
    g360: BSplineCurve PolesCount=2 KnotsCount=2 Degree=1 IsPeriodic=0
    g361: BSplineCurve PolesCount=2 KnotsCount=2 Degree=1 IsPeriodic=0
    g362: BSplineCurve PolesCount=4 KnotsCount=2 Degree=3 IsPeriodic=0
    g363: BSplineCurve PolesCount=4 KnotsCount=2 Degree=3 IsPeriodic=0
    g364: BSplineCurve PolesCount=4 KnotsCount=2 Degree=3 IsPeriodic=0
    g365: BSplineCurve PolesCount=4 KnotsCount=2 Degree=3 IsPeriodic=0
    g366: BSplineCurve PolesCount=4 KnotsCount=2 Degree=3 IsPeriodic=0
    g367: BSplineCurve PolesCount=4 KnotsCount=2 Degree=3 IsPeriodic=0
    g368: BSplineCurve PolesCount=4 KnotsCount=2 Degree=3 IsPeriodic=0
    g369: BSplineCurve PolesCount=4 KnotsCount=2 Degree=3 IsPeriodic=0
    g370: BSplineCurve PolesCount=4 KnotsCount=2 Degree=3 IsPeriodic=0
    g371: BSplineCurve PolesCount=4 KnotsCount=2 Degree=3 IsPeriodic=0
    g372: BSplineCurve PolesCount=4 KnotsCount=2 Degree=3 IsPeriodic=0
    g373: BSplineCurve PolesCount=2 KnotsCount=2 Degree=1 IsPeriodic=0
    g374: BSplineCurve PolesCount=4 KnotsCount=2 Degree=3 IsPeriodic=0
    g375: BSplineCurve PolesCount=4 KnotsCount=2 Degree=3 IsPeriodic=0
    g376: BSplineCurve PolesCount=4 KnotsCount=2 Degree=3 IsPeriodic=0
    g377: BSplineCurve PolesCount=4 KnotsCount=2 Degree=3 IsPeriodic=0
    g378: BSplineCurve PolesCount=4 KnotsCount=2 Degree=3 IsPeriodic=0
    g379: BSplineCurve PolesCount=4 KnotsCount=2 Degree=3 IsPeriodic=0
    g380: BSplineCurve PolesCount=4 KnotsCount=2 Degree=3 IsPeriodic=0
    g381: BSplineCurve PolesCount=4 KnotsCount=2 Degree=3 IsPeriodic=0
    g382: BSplineCurve PolesCount=4 KnotsCount=2 Degree=3 IsPeriodic=0
    g383: BSplineCurve PolesCount=4 KnotsCount=2 Degree=3 IsPeriodic=0
    g384: BSplineCurve PolesCount=4 KnotsCount=2 Degree=3 IsPeriodic=0
    g385: BSplineCurve PolesCount=4 KnotsCount=2 Degree=3 IsPeriodic=0
    g386: BSplineCurve PolesCount=4 KnotsCount=2 Degree=3 IsPeriodic=0
    g387: BSplineCurve PolesCount=2 KnotsCount=2 Degree=1 IsPeriodic=0
    g388: BSplineCurve PolesCount=4 KnotsCount=2 Degree=3 IsPeriodic=0
    g389: BSplineCurve PolesCount=4 KnotsCount=2 Degree=3 IsPeriodic=0
    g390: BSplineCurve PolesCount=4 KnotsCount=2 Degree=3 IsPeriodic=0
    g391: BSplineCurve PolesCount=4 KnotsCount=2 Degree=3 IsPeriodic=0
    g392: BSplineCurve PolesCount=4 KnotsCount=2 Degree=3 IsPeriodic=0
    g393: BSplineCurve PolesCount=4 KnotsCount=2 Degree=3 IsPeriodic=0
    g394: BSplineCurve PolesCount=4 KnotsCount=2 Degree=3 IsPeriodic=0
    g395: BSplineCurve PolesCount=4 KnotsCount=2 Degree=3 IsPeriodic=0
    g396: BSplineCurve PolesCount=4 KnotsCount=2 Degree=3 IsPeriodic=0
    g397: BSplineCurve PolesCount=4 KnotsCount=2 Degree=3 IsPeriodic=0
    g398: BSplineCurve PolesCount=4 KnotsCount=2 Degree=3 IsPeriodic=0
    g399: BSplineCurve PolesCount=4 KnotsCount=2 Degree=3 IsPeriodic=0
    ... +22 more geometry lines
  constraints (425):
    c: Coincident(g0,g1)
    c: Coincident(g1,g2)
    c: Coincident(g2,g3)
    c: Coincident(g3,g4)
    c: Coincident(g4,g5)
    c: Coincident(g5,g6)
    c: Coincident(g6,g7)
    c: Coincident(g7,g8)
    c: Coincident(g8,g9)
    c: Coincident(g9,g10)
    c: Coincident(g10,g11)
    c: Coincident(g11,g12)
    c: Coincident(g12,g13)
    c: Coincident(g13,g14)
    c: Coincident(g14,g15)
    c: Coincident(g15,g16)
    c: Coincident(g16,g17)
    c: Coincident(g17,g18)
    c: Coincident(g18,g19)
    c: Coincident(g19,g20)
    c: Coincident(g20,g21)
    c: Coincident(g21,g22)
    c: Coincident(g22,g23)
    c: Coincident(g23,g24)
    c: Coincident(g24,g25)
    c: Coincident(g25,g26)
    c: Coincident(g26,g27)
    c: Coincident(g27,g28)
    c: Coincident(g28,g29)
    c: Coincident(g29,g30)
    c: Coincident(g30,g31)
    c: Coincident(g31,g32)
    c: Coincident(g32,g33)
    c: Coincident(g33,g34)
    c: Coincident(g34,g35)
    c: Coincident(g35,g36)
    c: Coincident(g36,g37)
    c: Coincident(g37,g38)
    c: Coincident(g38,g39)
    c: Coincident(g39,g40)
    c: Coincident(g40,g41)
    c: Coincident(g41,g42)
    c: Coincident(g42,g43)
    c: Coincident(g43,g44)
    c: Coincident(g44,g45)
    c: Coincident(g45,g46)
    c: Coincident(g46,g47)
    c: Coincident(g47,g48)
    c: Coincident(g48,g49)
    c: Coincident(g49,g50)
    c: Coincident(g50,g51)
    c: Coincident(g51,g52)
    c: Coincident(g52,g53)
    c: Coincident(g53,g54)
    c: Coincident(g54,g55)
    c: Coincident(g55,g56)
    c: Coincident(g56,g57)
    c: Coincident(g57,g58)
    c: Coincident(g58,g59)
    c: Coincident(g59,g60)
    c: Coincident(g60,g61)
    c: Coincident(g61,g62)
    c: Coincident(g62,g63)
    c: Coincident(g63,g64)
    c: Coincident(g64,g65)
    c: Coincident(g65,g66)
    c: Coincident(g66,g67)
    c: Coincident(g67,g68)
    c: Coincident(g68,g69)
    c: Coincident(g69,g70)
    c: Coincident(g70,g71)
    c: Coincident(g71,g72)
    c: Coincident(g72,g73)
    c: Coincident(g73,g74)
    c: Coincident(g74,g75)
    c: Coincident(g75,g76)
    c: Coincident(g76,g77)
    c: Coincident(g77,g78)
    c: Coincident(g78,g79)
    c: Coincident(g79,g80)
    c: Coincident(g80,g81)
    c: Coincident(g81,g82)
    c: Coincident(g82,g83)
    c: Coincident(g83,g84)
    c: Coincident(g84,g85)
    c: Coincident(g85,g86)
    c: Coincident(g86,g87)
    c: Coincident(g87,g88)
    c: Coincident(g88,g89)
    c: Coincident(g89,g90)
    c: Coincident(g90,g91)
    c: Coincident(g91,g92)
    c: Coincident(g92,g93)
    c: Coincident(g93,g94)
    c: Coincident(g94,g95)
    c: Coincident(g95,g96)
    c: Coincident(g96,g97)
    c: Coincident(g97,g98)
    c: Coincident(g98,g99)
    c: Coincident(g99,g100)
    c: Coincident(g100,g101)
    c: Coincident(g101,g102)
    c: Coincident(g102,g103)
    c: Coincident(g103,g104)
    c: Coincident(g104,g105)
    c: Coincident(g105,g106)
    c: Coincident(g106,g107)
    c: Coincident(g107,g108)
    c: Coincident(g108,g109)
    c: Coincident(g109,g110)
    c: Coincident(g110,g111)
    c: Coincident(g111,g112)
    c: Coincident(g112,g113)
    c: Coincident(g113,g114)
    c: Coincident(g114,g115)
    c: Coincident(g115,g116)
    c: Coincident(g116,g117)
    c: Coincident(g117,g118)
    c: Coincident(g118,g119)
    c: Coincident(g119,g120)
    c: Coincident(g120,g121)
    c: Coincident(g121,g122)
    c: Coincident(g122,g123)
    c: Coincident(g123,g124)
    c: Coincident(g124,g125)
    c: Coincident(g125,g126)
    c: Coincident(g126,g127)
    c: Coincident(g127,g128)
    c: Coincident(g128,g129)
    c: Coincident(g129,g130)
    c: Coincident(g130,g131)
    c: Coincident(g131,g132)
    c: Coincident(g132,g133)
    c: Coincident(g133,g134)
    c: Coincident(g134,g135)
    c: Coincident(g135,g136)
    c: Coincident(g136,g137)
    c: Coincident(g137,g138)
    c: Coincident(g138,g139)
    c: Coincident(g139,g140)
    c: Coincident(g140,g141)
    c: Coincident(g141,g142)
    c: Coincident(g142,g143)
    c: Coincident(g143,g144)
    c: Coincident(g144,g145)
    c: Coincident(g145,g146)
    c: Coincident(g146,g147)
    c: Coincident(g147,g148)
    c: Coincident(g148,g149)
    c: Coincident(g149,g150)
    c: Coincident(g150,g151)
    c: Coincident(g151,g152)
    c: Coincident(g152,g153)
    c: Coincident(g153,g154)
    c: Coincident(g154,g155)
    c: Coincident(g155,g156)
    c: Coincident(g156,g157)
    c: Coincident(g157,g158)
    c: Coincident(g158,g159)
    c: Coincident(g159,g160)
    c: Coincident(g160,g161)
    c: Coincident(g161,g162)
    c: Coincident(g162,g163)
    c: Coincident(g163,g164)
    c: Coincident(g164,g165)
    c: Coincident(g165,g166)
    c: Coincident(g166,g167)
    c: Coincident(g167,g168)
    c: Coincident(g168,g169)
    c: Coincident(g169,g170)
    c: Coincident(g170,g171)
    c: Coincident(g171,g172)
    c: Coincident(g172,g173)
    c: Coincident(g173,g174)
    c: Coincident(g174,g175)
    c: Coincident(g175,g176)
    c: Coincident(g176,g177)
    c: Coincident(g177,g178)
    c: Coincident(g178,g179)
    c: Coincident(g179,g180)
    c: Coincident(g180,g181)
    c: Coincident(g181,g182)
    c: Coincident(g182,g183)
    c: Coincident(g183,g184)
    c: Coincident(g184,g185)
    c: Coincident(g185,g186)
    c: Coincident(g186,g187)
    c: Coincident(g187,g188)
    c: Coincident(g188,g189)
    c: Coincident(g189,g190)
    c: Coincident(g190,g0)
    c: Coincident(g191,g192)
    c: Coincident(g192,g193)
    c: Coincident(g193,g194)
    c: Coincident(g194,g195)
    c: Coincident(g195,g196)
    c: Coincident(g196,g197)
    c: Coincident(g197,g198)
    c: Coincident(g198,g199)
    c: Coincident(g199,g200)
    c: Coincident(g200,g201)
    c: Coincident(g201,g202)
    c: Coincident(g202,g203)
    c: Coincident(g203,g204)
    c: Coincident(g204,g205)
    c: Coincident(g205,g206)
    c: Coincident(g206,g207)
    c: Coincident(g207,g208)
    c: Coincident(g208,g209)
    c: Coincident(g209,g210)
    c: Coincident(g210,g211)
    c: Coincident(g211,g212)
    c: Coincident(g212,g213)
    c: Coincident(g213,g214)
    c: Coincident(g214,g191)
    c: Coincident(g215,g216)
    c: Coincident(g216,g217)
    c: Coincident(g217,g215)
    c: Coincident(g218,g219)
    c: Coincident(g219,g220)
    c: Coincident(g220,g218)
    c: Coincident(g221,g222)
    c: Coincident(g222,g223)
    c: Coincident(g224,g225)
    c: Coincident(g225,g221)
    c: Coincident(g226,g227)
    c: Coincident(g227,g228)
    c: Coincident(g228,g229)
    c: Coincident(g229,g230)
    c: Coincident(g230,g231)
    c: Coincident(g231,g232)
    c: Coincident(g232,g233)
    c: Coincident(g233,g234)
    c: Coincident(g234,g235)
    c: Coincident(g235,g236)
    c: Coincident(g236,g237)
    c: Coincident(g237,g238)
    c: Coincident(g238,g226)
    c: Coincident(g239,g240)
    c: Coincident(g240,g241)
    c: Coincident(g241,g242)
    c: Coincident(g242,g243)
    c: Coincident(g243,g244)
    c: Coincident(g244,g245)
    c: Coincident(g245,g246)
    c: Coincident(g246,g247)
    c: Coincident(g247,g248)
    c: Coincident(g248,g239)
    c: Coincident(g249,g250)
    c: Coincident(g250,g251)
    c: Coincident(g251,g252)
    c: Coincident(g252,g249)
    c: Coincident(g253,g254)
    c: Coincident(g254,g255)
    c: Coincident(g255,g253)
    c: Coincident(g256,g257)
    c: Coincident(g257,g258)
    c: Coincident(g258,g259)
    c: Coincident(g259,g260)
    c: Coincident(g260,g261)
    c: Coincident(g261,g256)
    c: Coincident(g262,g263)
    c: Coincident(g263,g264)
    c: Coincident(g264,g265)
    c: Coincident(g265,g262)
    c: Coincident(g266,g267)
    c: Coincident(g267,g268)
    c: Coincident(g268,g269)
    c: Coincident(g269,g270)
    c: Coincident(g270,g271)
    c: Coincident(g271,g272)
    c: Coincident(g272,g273)
    c: Coincident(g273,g274)
    c: Coincident(g274,g275)
    c: Coincident(g275,g276)
    c: Coincident(g276,g277)
    c: Coincident(g277,g278)
    c: Coincident(g278,g279)
    c: Coincident(g279,g280)
    c: Coincident(g280,g281)
    c: Coincident(g281,g282)
    c: Coincident(g282,g283)
    c: Coincident(g283,g284)
    c: Coincident(g284,g285)
    c: Coincident(g285,g266)
    c: Coincident(g286,g287)
    c: Coincident(g287,g288)
    c: Coincident(g288,g289)
    c: Coincident(g289,g290)
    c: Coincident(g290,g291)
    c: Coincident(g291,g286)
    c: Coincident(g292,g293)
    c: Coincident(g293,g294)
    c: Coincident(g294,g295)
    c: Coincident(g295,g296)
    c: Coincident(g296,g297)
    c: Coincident(g297,g298)
    c: Coincident(g298,g299)
    c: Coincident(g299,g300)
    c: Coincident(g300,g301)
    c: Coincident(g301,g302)
    c: Coincident(g302,g303)
    c: Coincident(g303,g304)
    c: Coincident(g304,g305)
    c: Coincident(g305,g306)
    c: Coincident(g306,g307)
    c: Coincident(g307,g308)
    c: Coincident(g308,g292)
    c: Coincident(g309,g310)
    c: Coincident(g310,g311)
    c: Coincident(g311,g309)
    c: Coincident(g312,g313)
    c: Coincident(g313,g314)
    c: Coincident(g314,g315)
    c: Coincident(g315,g316)
    c: Coincident(g316,g317)
    c: Coincident(g317,g318)
    c: Coincident(g318,g319)
    c: Coincident(g319,g320)
    c: Coincident(g320,g321)
    c: Coincident(g321,g322)
    c: Coincident(g322,g323)
    c: Coincident(g323,g324)
    c: Coincident(g324,g325)
    c: Coincident(g325,g326)
    c: Coincident(g326,g327)
    c: Coincident(g327,g328)
    c: Coincident(g328,g329)
    c: Coincident(g329,g330)
    c: Coincident(g330,g331)
    c: Coincident(g331,g332)
    c: Coincident(g332,g333)
    c: Coincident(g333,g334)
    c: Coincident(g334,g335)
    c: Coincident(g335,g336)
    c: Coincident(g336,g312)
    c: Coincident(g337,g338)
    c: Coincident(g338,g339)
    c: Coincident(g339,g340)
    c: Coincident(g340,g341)
    c: Coincident(g341,g342)
    c: Coincident(g342,g343)
    c: Coincident(g343,g344)
    c: Coincident(g344,g345)
    c: Coincident(g345,g337)
    c: Coincident(g346,g347)
    c: Coincident(g347,g348)
    c: Coincident(g348,g349)
    c: Coincident(g349,g350)
    c: Coincident(g350,g351)
    c: Coincident(g351,g352)
    c: Coincident(g352,g353)
    c: Coincident(g353,g354)
    c: Coincident(g354,g355)
    c: Coincident(g355,g346)
    c: Coincident(g356,g357)
    c: Coincident(g357,g358)
    c: Coincident(g358,g359)
    c: Coincident(g359,g360)
    c: Coincident(g360,g361)
    c: Coincident(g361,g362)
    c: Coincident(g362,g363)
    c: Coincident(g363,g364)
    c: Coincident(g364,g365)
    c: Coincident(g365,g366)
    c: Coincident(g366,g367)
    c: Coincident(g367,g368)
    c: Coincident(g368,g369)
    c: Coincident(g369,g370)
    c: Coincident(g370,g371)
    c: Coincident(g371,g372)
    c: Coincident(g372,g373)
    c: Coincident(g373,g356)
    c: Coincident(g374,g375)
    c: Coincident(g375,g376)
    c: Coincident(g376,g374)
    c: Coincident(g377,g378)
    c: Coincident(g378,g379)
    c: Coincident(g379,g380)
    c: Coincident(g380,g381)
    c: Coincident(g381,g377)
    c: Coincident(g382,g383)
    c: Coincident(g383,g384)
    c: Coincident(g384,g385)
    c: Coincident(g385,g386)
    c: Coincident(g386,g387)
    c: Coincident(g387,g382)
    c: Coincident(g388,g389)
    c: Coincident(g389,g390)
    c: Coincident(g390,g391)
    c: Coincident(g391,g392)
    c: Coincident(g392,g393)
    c: Coincident(g393,g388)
    c: Coincident(g394,g395)
    c: Coincident(g395,g396)
    c: Coincident(g396,g397)
    c: Coincident(g397,g394)
    c: Coincident(g398,g399)
    c: Coincident(g399,g400)
    c: Coincident(g400,g401)
    c: Coincident(g401,g402)
    c: Coincident(g402,g398)
    c: Coincident(g403,g404)
    c: Coincident(g404,g405)
    c: Coincident(g405,g406)
    c: Coincident(g406,g407)
    c: Coincident(g407,g408)
    c: Coincident(g408,g409)
    c: Coincident(g409,g410)
    c: Coincident(g410,g411)
    c: Coincident(g411,g412)
    c: Coincident(g412,g413)
    c: Coincident(g413,g414)
    c: Coincident(g414,g415)
    c: Coincident(g415,g403)
    c: Weight(g416) = 1
    c: Equal(g416,g417)
    c: Equal(g416,g418)
    c: InternalAlignment(g416,g419)
    c: InternalAlignment(g417,g419)
    c: InternalAlignment(g418,g419)
    c: InternalAlignment(g420,g419)
    c: InternalAlignment(g421,g419)
    c: Coincident(g419,g224)
    c: Coincident(g419,g223)
FEATURE [Sketcher::SketchObject] Sketch018  label="Rectangle"
  FullyConstrained = false
  MapMode = 5
  Support = -> [XY_Plane]
  sketch-geometry (4):
    g0: LineSegment StartX=20.9677 StartY=-89.8282 StartZ=0 EndX=203.659 EndY=-89.8282 EndZ=0
    g1: LineSegment StartX=203.659 StartY=-89.8282 StartZ=0 EndX=203.659 EndY=-211.827 EndZ=0
    g2: LineSegment StartX=203.659 StartY=-211.827 StartZ=0 EndX=20.9677 EndY=-211.827 EndZ=0
    g3: LineSegment StartX=20.9677 StartY=-211.827 StartZ=0 EndX=20.9677 EndY=-89.8282 EndZ=0
  constraints (8):
    c: Coincident(g0,g1)
    c: Coincident(g1,g2)
    c: Coincident(g2,g3)
    c: Coincident(g3,g0)
    c: Horizontal(g0)
    c: Horizontal(g2)
    c: Vertical(g1)
    c: Vertical(g3)
FEATURE [PartDesign::Pad] Pad
  Direction = (1,1,1)
  Length = 10
  Length2 = 100
  Profile = -> Sketch018
  Reversed = true
  Type = 0
FEATURE [PartDesign::Pocket] Pocket  label="Pocket-House"
  BaseFeature = -> Pad
  Length = 2
  Length2 = 100
  Profile = -> Sketch017
  Type = 0
FEATURE [PartDesign::Pocket] Pocket001  label="Pocket-A"
  BaseFeature = -> Pocket
  Length = 2
  Length2 = 100
  Profile = -> Sketch015
  Type = 0
FEATURE [PartDesign::Pocket] Pocket002  label="Pocket-S002"
  BaseFeature = -> Pocket001
  Length = 2
  Length2 = 100
  Profile = -> Sketch016
  Type = 0
FEATURE [PartDesign::Pocket] Pocket003  label="Pocket-L"
  BaseFeature = -> Pocket002
  Length = 2
  Length2 = 100
  Profile = -> Sketch014
  Type = 0
FEATURE [PartDesign::Pocket] Pocket004  label="Pocket-E002"
  BaseFeature = -> Pocket003
  Length = 2
  Length2 = 100
  Profile = -> Sketch013
  Type = 0
FEATURE [PartDesign::Pocket] Pocket005  label="Pocket-O"
  BaseFeature = -> Pocket004
  Length = 2
  Length2 = 100
  Profile = -> Sketch012
  Type = 0
FEATURE [PartDesign::Pocket] Pocket006  label="Pocket-T"
  BaseFeature = -> Pocket005
  Length = 2
  Length2 = 100
  Profile = -> Sketch011
  Type = 0
FEATURE [PartDesign::Pocket] Pocket007  label="Pocket-D001"
  BaseFeature = -> Pocket006
  Length = 2
  Length2 = 100
  Profile = -> Sketch010
  Type = 0
FEATURE [PartDesign::Pocket] Pocket008  label="Pocket-N001"
  BaseFeature = -> Pocket007
  Length = 2
  Length2 = 100
  Profile = -> Sketch009
  Type = 0
FEATURE [PartDesign::Pocket] Pocket009  label="Pocket-G"
  BaseFeature = -> Pocket008
  Length = 2
  Length2 = 100
  Profile = -> Sketch008
  Type = 0
FEATURE [PartDesign::Pocket] Pocket010  label="Pocket-D"
  BaseFeature = -> Pocket009
  Length = 2
  Length2 = 100
  Profile = -> Sketch007
  Type = 0
FEATURE [PartDesign::Pocket] Pocket011  label="Pocket-E001"
  BaseFeature = -> Pocket010
  Length = 2
  Length2 = 100
  Profile = -> Sketch006
  Type = 0
FEATURE [PartDesign::Pocket] Pocket012  label="Pocket-H"
  BaseFeature = -> Pocket011
  Length = 2
  Length2 = 100
  Profile = -> Sketch005
  Type = 0
FEATURE [PartDesign::Pocket] Pocket013  label="Pocket-E"
  BaseFeature = -> Pocket012
  Length = 2
  Length2 = 100
  Profile = -> Sketch004
  Type = 0
FEATURE [PartDesign::Pocket] Pocket014  label="Pocket-S001"
  BaseFeature = -> Pocket013
  Length = 2
  Length2 = 100
  Profile = -> Sketch003
  Type = 0
FEATURE [PartDesign::Pocket] Pocket015  label="Pocket-S"
  BaseFeature = -> Pocket014
  Length = 2
  Length2 = 100
  Profile = -> Sketch002
  Type = 0
FEATURE [PartDesign::Pocket] Pocket016  label="Pocket-N"
  BaseFeature = -> Pocket015
  Length = 2
  Length2 = 100
  Profile = -> Sketch001
  Type = 0
FEATURE [PartDesign::Pocket] Pocket017  label="Pocket-M"
  BaseFeature = -> Pocket016
  Length = 2
  Length2 = 100
  Profile = -> Sketch
  Type = 0
FEATURE [Sketcher::SketchObject] Sketch019
  FullyConstrained = false
  MapMode = 5
  Support = -> [XY_Plane]
  sketch-geometry (3):
    g0: LineSegment StartX=99.0992 StartY=-168.585 StartZ=0 EndX=98.898 EndY=-170.899 EndZ=0
    g1: LineSegment StartX=98.898 StartY=-170.899 StartZ=0 EndX=100.709 EndY=-168.585 EndZ=0
    g2: LineSegment StartX=100.709 StartY=-168.585 StartZ=0 EndX=99.0992 EndY=-168.585 EndZ=0
  constraints (3):
    c: Coincident(g0,g1)
    c: Coincident(g1,g2)
    c: Coincident(g2,g0)
FEATURE [PartDesign::Pocket] Pocket018  label="Pocket-Apos"
  BaseFeature = -> Pocket017
  Length = 2
  Length2 = 100
  Profile = -> Sketch019
  Type = 0
FEATURE [PartDesign::Body] Body  label="Body163x108"
  Group = -> [Sketch017,Sketch018,Pad,Pocket,Sketch015,Pocket001,Sketch016,Pocket002,Sketch014,Pocket003,Sketch013,Pocket004,Sketch012,Pocket005,Sketch011,Pocket006,Sketch010,Pocket007,Sketch009,Pocket008,Sketch008,Pocket009,Sketch007,Pocket010,Sketch006,Pocket011,Sketch005,Pocket012,Sketch004,Pocket013,Sketch003,Pocket014,Sketch002,Pocket015,Sketch001,Pocket016,Sketch,Pocket017,Sketch019,Pocket018]
  Origin = -> Origin
  Placement = pos=(-109,153,0) rot=(0,0,1;0rad)
  Tip = -> Pocket018
FEATURE [Part::FeaturePython] Clone001  label="Body90"  # Draft clone (typed FeaturePython)
  AttacherType = Attacher::AttachEngine3D
  Fuse = false
  Objects = -> [Body]
  Placement = pos=(-92,128,0) rot=(0,0,1;0rad)
  Scale = (0.85,0.85,1)
FEATURE [App::FeaturePython] SetupSheet  # Path/CAM operation (typed FeaturePython)
  ClearanceHeightExpression = OpStockZMax+SetupSheet.ClearanceHeightOffset
  ClearanceHeightOffset = 5
  CoolantMode = 0
  CoolantModes = None | Flood | Mist
  FinalDepthExpression = OpFinalDepth
  HorizRapid = 0
  SafeHeightExpression = OpStockZMax+SetupSheet.SafeHeightOffset
  SafeHeightOffset = 3
  StartDepthExpression = OpStartDepth
  StepDownExpression = OpToolDiameter
  VertRapid = 0
FEATURE [Part::FeaturePython] Clone  label="Model-Body163x108"  # Draft clone (typed FeaturePython)
  AttacherType = Attacher::AttachEngine3D
  Fuse = false
  Objects = -> [Body]
  PathResource = Model
  Placement = pos=(-109,153,0) rot=(0,0,1;0rad)
  Scale = (1,1,1)
FEATURE [App::DocumentObjectGroup] Model
  Group = -> [Clone]
FEATURE [Part::FeaturePython] Stock001  # WARN: FeaturePython — macro-defined, semantics opaque (R4)
  Height = 10
  Length = 182.69
  Placement = pos=(-88.0323,-58.8273,-10) rot=(0,0,1;0rad)
  StockType = CreateBox
  Width = 121.999
FEATURE [Part::FeaturePython] ToolBit001  label="60 Deg. V-Bit"  # Path/CAM toolbit (typed FeaturePython)
  BitPropertyNames = Chipload | CuttingEdgeAngle | CuttingEdgeHeight | Diameter | Flutes | Length | Material | ShankDiameter | TipDiameter
  BitShape = <path>
  Chipload = 0
  CuttingEdgeAngle = 60
  CuttingEdgeHeight = 1
  Diameter = 10
  File = <userpath>/MensShed/CNCRouter/FreeCAD/Bit/60degree_Vbit.fctb
  Flutes = 0
  Length = 20
  Material = 0
  ShankDiameter = 5
  ShapeName = v_bit
  TipDiameter = 1
FEATURE [Path::FeaturePython] _0_Deg__V_Bit  label="60 Deg. V-Bit001"  # Path/CAM operation (typed FeaturePython)
  HorizFeed = 15
  HorizRapid = 0
  SpindleDir = 0
  SpindleSpeed = 15000
  Tool = -> ToolBit001
  ToolNumber = 2
  VertFeed = 5
  VertRapid = 0
  expr: HorizRapid = SetupSheet.HorizRapid
  expr: VertRapid = SetupSheet.VertRapid
FEATURE [Path::FeaturePython] Vcarve001  # Path/CAM operation (typed FeaturePython)
  Active = true
  Base = -> [Clone]
  ClearanceHeight = 5
  Colinear = 10
  CoolantMode = None
  CycleTime = 00:08:24
  Discretize = 0.01
  FinalDepth = -10
  OpFinalDepth = -10
  OpStartDepth = 0
  OpStockZMax = 0
  OpStockZMin = -10
  OpToolDiameter = 10
  SafeHeight = 3
  StartDepth = 0
  Tolerance = 0.01
  ToolController = -> _0_Deg__V_Bit
  expr: ClearanceHeight = OpStockZMax + SetupSheet.ClearanceHeightOffset
  expr: SafeHeight = OpStockZMax + SetupSheet.SafeHeightOffset
  expr: FinalDepth = OpFinalDepth
  expr: StartDepth = OpStartDepth
FEATURE [App::FeaturePython] SetupSheet001  # Path/CAM operation (typed FeaturePython)
  ClearanceHeightExpression = OpStockZMax+SetupSheet001.ClearanceHeightOffset
  ClearanceHeightOffset = 5
  CoolantMode = 0
  CoolantModes = None | Flood | Mist
  FinalDepthExpression = OpFinalDepth
  HorizRapid = 0
  SafeHeightExpression = OpStockZMax+SetupSheet001.SafeHeightOffset
  SafeHeightOffset = 3
  StartDepthExpression = OpStartDepth
  StepDownExpression = OpToolDiameter
  VertRapid = 0
FEATURE [Part::FeaturePython] Clone002  label="Model-Body90"  # Draft clone (typed FeaturePython)
  AttacherType = Attacher::AttachEngine3D
  Fuse = false
  Objects = -> [Clone001]
  PathResource = Model
  Placement = pos=(-92,128,0) rot=(0,0,1;0rad)
  Scale = (1,1,1)
FEATURE [App::DocumentObjectGroup] Model001
  Group = -> [Clone002]
FEATURE [Part::FeaturePython] Stock002  # WARN: FeaturePython — macro-defined, semantics opaque (R4)
  Height = 10
  Length = 155.29
  Placement = pos=(-74.1775,-52.0532,-10) rot=(0,0,1;0rad)
  StockType = CreateBox
  Width = 103.699
FEATURE [Part::FeaturePython] ToolBit002  label="60 Deg. V-Bit002"  # Path/CAM toolbit (typed FeaturePython)
  BitPropertyNames = Chipload | CuttingEdgeAngle | CuttingEdgeHeight | Diameter | Flutes | Length | Material | ShankDiameter | TipDiameter
  BitShape = <path>
  Chipload = 0
  CuttingEdgeAngle = 60
  CuttingEdgeHeight = 1
  Diameter = 10
  File = <userpath>/MensShed/CNCRouter/FreeCAD/Bit/60degree_Vbit.fctb
  Flutes = 0
  Length = 20
  Material = 0
  ShankDiameter = 5
  ShapeName = v_bit
  TipDiameter = 1
FEATURE [Path::FeaturePython] _0_Deg__V_Bit002  label="60 Deg. V-Bit003"  # Path/CAM operation (typed FeaturePython)
  HorizFeed = 15
  HorizRapid = 0
  SpindleDir = 0
  SpindleSpeed = 15000
  Tool = -> ToolBit002
  ToolNumber = 2
  VertFeed = 5
  VertRapid = 0
  expr: HorizRapid = SetupSheet001.HorizRapid
  expr: VertRapid = SetupSheet001.VertRapid
FEATURE [App::DocumentObjectGroup] Tools001
  Group = -> [_0_Deg__V_Bit002]
FEATURE [Path::FeaturePython] Vcarve002  # Path/CAM operation (typed FeaturePython)
  Active = true
  Base = -> [Clone002]
  ClearanceHeight = 5
  Colinear = 10
  CoolantMode = None
  CycleTime = 00:09:21
  Discretize = 0.01
  FinalDepth = -10
  OpFinalDepth = -10
  OpStartDepth = 0
  OpStockZMax = 0
  OpStockZMin = -10
  OpToolDiameter = 10
  SafeHeight = 3
  StartDepth = 0
  Tolerance = 0.01
  ToolController = -> _0_Deg__V_Bit002
  expr: ClearanceHeight = OpStockZMax + SetupSheet001.ClearanceHeightOffset
  expr: SafeHeight = OpStockZMax + SetupSheet001.SafeHeightOffset
  expr: FinalDepth = OpFinalDepth
  expr: StartDepth = OpStartDepth
FEATURE [Path::FeaturePython] Vcarve003  # Path/CAM operation (typed FeaturePython)
  Active = true
  Base = -> [Clone002]
  ClearanceHeight = 5
  Colinear = 10
  CoolantMode = None
  CycleTime = 00:07:39
  Discretize = 0.01
  FinalDepth = -10
  OpFinalDepth = -10
  OpStartDepth = 0
  OpStockZMax = 0
  OpStockZMin = -10
  OpToolDiameter = 10
  SafeHeight = 3
  StartDepth = 0
  Tolerance = 0.01
  ToolController = -> _0_Deg__V_Bit002
  expr: ClearanceHeight = OpStockZMax + SetupSheet001.ClearanceHeightOffset
  expr: SafeHeight = OpStockZMax + SetupSheet001.SafeHeightOffset
  expr: FinalDepth = OpFinalDepth
  expr: StartDepth = OpStartDepth
FEATURE [Path::FeatureCompoundPython] Operations001  # Path/CAM operation (typed FeaturePython)
  Group = -> [Vcarve002,Vcarve003]
  UsePlacements = false
FEATURE [Path::FeaturePython] Job001  label="JobSmall"  # Path/CAM operation (typed FeaturePython)
  CycleTime = 00:17:00
  Fixtures = G54
  GeometryTolerance = 0.01
  LastPostProcessDate = 2022-04-15 16:08:35.474439
  LastPostProcessOutput = <userpath>/MensShed/CNCRouter/Shapes/MensShedLogoVBitSmall.ngc
  Model = -> Model001
  Operations = -> Operations001
  OrderOutputBy = 0
  PostProcessor = 2
  PostProcessorOutputFile = %D/%dSmall.ngc
  SetupSheet = -> SetupSheet001
  SplitOutput = false
  Stock = -> Stock002
  Tools = -> Tools001
FEATURE [Mesh::FeaturePython] CutMaterial  # WARN: FeaturePython — macro-defined, semantics opaque (R4)
FEATURE [Mesh::FeaturePython] CutMaterialIn  # WARN: FeaturePython — macro-defined, semantics opaque (R4)
FEATURE [App::FeaturePython] SetupSheet002  # Path/CAM operation (typed FeaturePython)
  ClearanceHeightExpression = OpStockZMax+SetupSheet002.ClearanceHeightOffset
  ClearanceHeightOffset = 5
  CoolantMode = 0
  CoolantModes = None | Flood | Mist
  FinalDepthExpression = OpFinalDepth
  HorizRapid = 0
  SafeHeightExpression = OpStockZMax+SetupSheet002.SafeHeightOffset
  SafeHeightOffset = 3
  StartDepthExpression = OpStartDepth
  StepDownExpression = OpToolDiameter
  VertRapid = 0
FEATURE [Part::FeaturePython] Clone003  label="Model-Body163x109"  # Draft clone (typed FeaturePython)
  AttacherType = Attacher::AttachEngine3D
  Fuse = false
  Objects = -> [Body]
  PathResource = Model
  Placement = pos=(-109,153,0) rot=(0,0,1;0rad)
  Scale = (1,1,1)
FEATURE [App::DocumentObjectGroup] Model002
  Group = -> [Clone003]
FEATURE [Part::FeaturePython] Stock003  # WARN: FeaturePython — macro-defined, semantics opaque (R4)
  Height = 10
  Length = 182.69
  Placement = pos=(-88.0323,-58.8273,-10) rot=(0,0,1;0rad)
  StockType = CreateBox
  Width = 121.999
FEATURE [Part::FeaturePython] ToolBit  label="90degree_Vbit002"  # Path/CAM toolbit (typed FeaturePython)
  BitPropertyNames = Chipload | CuttingEdgeAngle | CuttingEdgeHeight | Diameter | Flutes | Length | Material | ShankDiameter | TipDiameter
  BitShape = <path>
  Chipload = 0
  CuttingEdgeAngle = 90
  CuttingEdgeHeight = 10
  Diameter = 20
  File = <userpath>/MensShed/CNCRouter/FreeCAD/Bit/90degree_Vbit.fctb
  Flutes = 0
  Length = 63
  Material = 0
  ShankDiameter = 12.7
  ShapeName = v_bit
  TipDiameter = 0.1
FEATURE [Path::FeaturePython] _0degree_Vbit002  label="90degree_Vbit003"  # Path/CAM operation (typed FeaturePython)
  HorizFeed = 10
  HorizRapid = 0
  SpindleDir = 0
  SpindleSpeed = 15000
  Tool = -> ToolBit
  ToolNumber = 3
  VertFeed = 5
  VertRapid = 0
  expr: HorizRapid = SetupSheet002.HorizRapid
  expr: VertRapid = SetupSheet002.VertRapid
FEATURE [App::DocumentObjectGroup] Tools002
  Group = -> [_0degree_Vbit002]
FEATURE [Path::FeaturePython] Vcarve004  # Path/CAM operation (typed FeaturePython)
  Active = true
  Base = -> [Clone003]
  ClearanceHeight = 5
  Colinear = 10
  CoolantMode = None
  CycleTime = 00:10:08
  Discretize = 0.01
  FinalDepth = -10
  OpFinalDepth = -10
  OpStartDepth = 0
  OpStockZMax = 0
  OpStockZMin = -10
  OpToolDiameter = 20
  SafeHeight = 3
  StartDepth = 0
  Tolerance = 0.01
  ToolController = -> _0degree_Vbit002
  expr: ClearanceHeight = OpStockZMax + SetupSheet002.ClearanceHeightOffset
  expr: SafeHeight = OpStockZMax + SetupSheet002.SafeHeightOffset
  expr: FinalDepth = OpFinalDepth
  expr: StartDepth = OpStartDepth
FEATURE [Path::FeatureCompoundPython] Operations002  # Path/CAM operation (typed FeaturePython)
  Group = -> [Vcarve004]
  UsePlacements = false
FEATURE [Path::FeaturePython] Job002  label="JobText"  # Path/CAM operation (typed FeaturePython)
  CycleTime = 00:10:08
  Fixtures = G54
  GeometryTolerance = 0.01
  LastPostProcessDate = 2022-04-20 09:58:00.754618
  LastPostProcessOutput = <userpath>/MensShed/CNCRouter/Shapes/MensShedLogoVBitText001.ngc
  Model = -> Model002
  Operations = -> Operations002
  OrderOutputBy = 0
  PostProcessor = 2
  PostProcessorOutputFile = %D/%dText.ngc
  SetupSheet = -> SetupSheet002
  SplitOutput = false
  Stock = -> Stock003
  Tools = -> Tools002
FEATURE [Part::FeaturePython] ToolBit003  label="90degree_Vbit004"  # Path/CAM toolbit (typed FeaturePython)
  BitPropertyNames = Chipload | CuttingEdgeAngle | CuttingEdgeHeight | Diameter | Flutes | Length | Material | ShankDiameter | TipDiameter
  BitShape = <path>
  Chipload = 0
  CuttingEdgeAngle = 90
  CuttingEdgeHeight = 10
  Diameter = 20
  File = <userpath>/MensShed/CNCRouter/FreeCAD/Bit/90degree_Vbit.fctb
  Flutes = 0
  Length = 63
  Material = 0
  ShankDiameter = 12.7
  ShapeName = v_bit
  TipDiameter = 0.1
FEATURE [Path::FeaturePython] _0degree_Vbit004  label="90degree_Vbit005"  # Path/CAM operation (typed FeaturePython)
  HorizFeed = 10
  HorizRapid = 0
  SpindleDir = 0
  SpindleSpeed = 15000
  Tool = -> ToolBit003
  ToolNumber = 3
  VertFeed = 5
  VertRapid = 0
  expr: HorizRapid = SetupSheet.HorizRapid
  expr: VertRapid = SetupSheet.VertRapid
FEATURE [App::DocumentObjectGroup] Tools
  Group = -> [_0_Deg__V_Bit,_0degree_Vbit004]
FEATURE [Path::FeaturePython] Vcarve  # Path/CAM operation (typed FeaturePython)
  Active = true
  Base = -> [Clone]
  ClearanceHeight = 5
  Colinear = 10
  CoolantMode = None
  CycleTime = 00:10:08
  Discretize = 0.01
  FinalDepth = -10
  OpFinalDepth = -10
  OpStartDepth = 0
  OpStockZMax = 0
  OpStockZMin = -10
  OpToolDiameter = 20
  SafeHeight = 3
  StartDepth = 0
  Tolerance = 0.01
  ToolController = -> _0degree_Vbit004
  expr: ClearanceHeight = OpStockZMax + SetupSheet.ClearanceHeightOffset
  expr: SafeHeight = OpStockZMax + SetupSheet.SafeHeightOffset
  expr: FinalDepth = OpFinalDepth
  expr: StartDepth = OpStartDepth
FEATURE [Path::FeatureCompoundPython] Operations  # Path/CAM operation (typed FeaturePython)
  Group = -> [Vcarve,Vcarve001]
  UsePlacements = false
FEATURE [Path::FeaturePython] Job  label="JobLarge"  # Path/CAM operation (typed FeaturePython)
  CycleTime = 00:18:32
  Fixtures = G54
  GeometryTolerance = 0.01
  LastPostProcessDate = 2022-04-15 16:09:24.507449
  LastPostProcessOutput = <userpath>/MensShed/CNCRouter/Shapes/MensShedLogoVBitLarge.ngc
  Model = -> Model
  Operations = -> Operations
  OrderOutputBy = 0
  PostProcessor = 2
  PostProcessorOutputFile = %D/%dLarge.ngc
  SetupSheet = -> SetupSheet
  SplitOutput = false
  Stock = -> Stock001
  Tools = -> Tools
note: 4 file-system paths scrubbed to <path> (originals preserved in the JSON sidecar)
